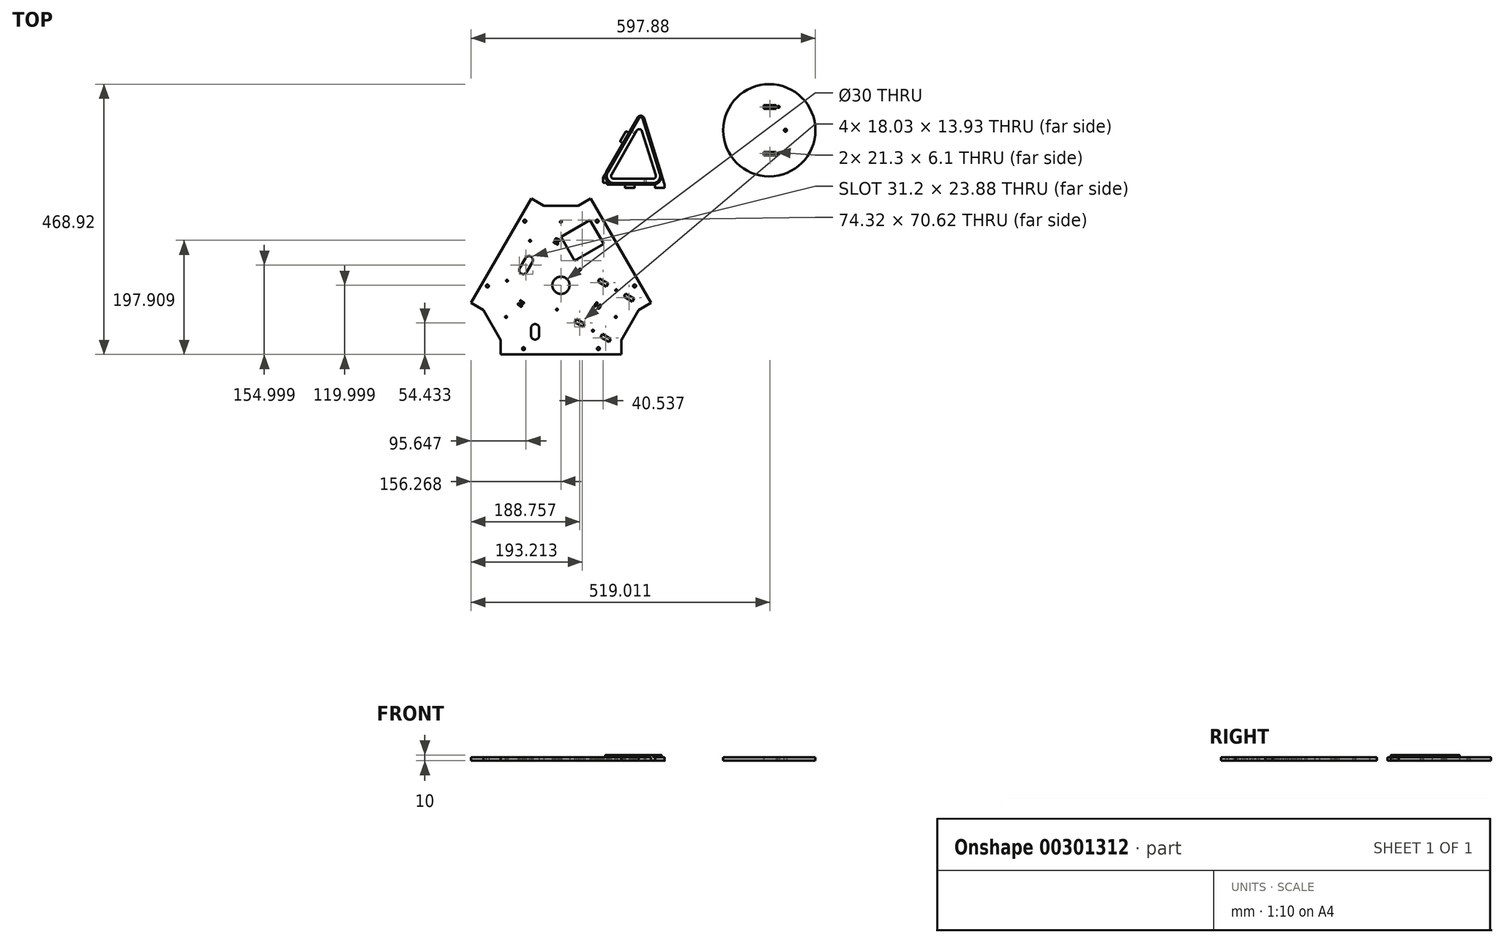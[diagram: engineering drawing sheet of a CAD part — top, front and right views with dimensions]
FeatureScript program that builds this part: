
annotation { "Feature Type Name" : "Feature", "Feature Type Description" : "" }
export const myFeature = defineFeature(function(context is Context, id is Id, definition is map)
    precondition{}
    {
        {
            var Q0;
            Q0=qCreatedBy(makeId("Top.planeOp"),FACE);
            var sketch = newSketch(context, id + "F0", { "sketchPlane" : qUnion([Q0])});
            skCircle(sketch, "E0", {"center": v(-173.6, -123.38) * mm, "radius": 80 * mm});
            skCircle(sketch, "E1", {"center": v(-45.84, -124.67) * mm, "radius": 2.5 * mm});
            skCircle(sketch, "E2", {"center": v(-110.84, -12.09) * mm, "radius": 2.5 * mm});
            skArc(sketch, "E3", {"start": v(-30.8, -243.38) * mm, "mid": v(-29.38, -242.8) * mm, "end": v(-28.8, -241.38) * mm});
            skLineSegment(sketch, "E4", {"start": v(-316.4, -243.38) * mm, "end": v(-30.8, -243.38) * mm});
            skArc(sketch, "E5", {"start": v(-318.4, -241.38) * mm, "mid": v(-317.81, -242.8) * mm, "end": v(-316.4, -243.38) * mm});
            skLineSegment(sketch, "E6", {"start": v(-318.4, -241.38) * mm, "end": v(-318.4, -221.41) * mm});
            skArc(sketch, "E7", {"start": v(-317.9, -220.55) * mm, "mid": v(-318.26, -220.91) * mm, "end": v(-318.4, -221.41) * mm});
            skLineSegment(sketch, "E8", {"start": v(-317.9, -220.55) * mm, "end": v(-299.77, -210.08) * mm});
            skLineSegment(sketch, "E9", {"start": v(-299.77, -210.08) * mm, "end": v(-311.77, -189.3) * mm});
            skLineSegment(sketch, "E10", {"start": v(-311.77, -189.3) * mm, "end": v(-329.9, -199.76) * mm});
            skArc(sketch, "E11", {"start": v(-330.9, -199.76) * mm, "mid": v(-330.4, -199.9) * mm, "end": v(-329.9, -199.76) * mm});
            skLineSegment(sketch, "E12", {"start": v(-348.19, -189.78) * mm, "end": v(-330.9, -199.76) * mm});
            skArc(sketch, "E13", {"start": v(-348.92, -187.05) * mm, "mid": v(-349.12, -188.57) * mm, "end": v(-348.19, -189.78) * mm});
            skLineSegment(sketch, "E14", {"start": v(-206.12, 60.29) * mm, "end": v(-348.92, -187.05) * mm});
            skLineSegment(sketch, "E15", {"start": v(-203.39, 61.02) * mm, "end": v(-186.1, 51.04) * mm});
            skArc(sketch, "E16", {"start": v(-185.6, 50.17) * mm, "mid": v(-185.73, 50.67) * mm, "end": v(-186.1, 51.04) * mm});
            skLineSegment(sketch, "E17", {"start": v(-185.6, 50.17) * mm, "end": v(-185.6, 29.24) * mm});
            skLineSegment(sketch, "E18", {"start": v(-185.6, 29.24) * mm, "end": v(-161.6, 29.24) * mm});
            skLineSegment(sketch, "E19", {"start": v(-161.6, 29.24) * mm, "end": v(-161.6, 50.17) * mm});
            skArc(sketch, "E20", {"start": v(-161.1, 51.04) * mm, "mid": v(-161.46, 50.67) * mm, "end": v(-161.6, 50.17) * mm});
            skLineSegment(sketch, "E21", {"start": v(-143.8, 61.02) * mm, "end": v(-161.1, 51.04) * mm});
            skLineSegment(sketch, "E22", {"start": v(1.72, -187.05) * mm, "end": v(-141.08, 60.29) * mm});
            skArc(sketch, "E23", {"start": v(1, -189.78) * mm, "mid": v(1.92, -188.57) * mm, "end": v(1.72, -187.05) * mm});
            skLineSegment(sketch, "E24", {"start": v(1, -189.78) * mm, "end": v(-16.3, -199.76) * mm});
            skArc(sketch, "E25", {"start": v(-17.3, -199.76) * mm, "mid": v(-16.8, -199.9) * mm, "end": v(-16.3, -199.76) * mm});
            skLineSegment(sketch, "E26", {"start": v(-17.3, -199.76) * mm, "end": v(-35.43, -189.3) * mm});
            skLineSegment(sketch, "E27", {"start": v(-35.43, -189.3) * mm, "end": v(-47.43, -210.08) * mm});
            skLineSegment(sketch, "E28", {"start": v(-47.43, -210.08) * mm, "end": v(-29.3, -220.55) * mm});
            skArc(sketch, "E29", {"start": v(-28.8, -221.41) * mm, "mid": v(-28.93, -220.91) * mm, "end": v(-29.3, -220.55) * mm});
            skLineSegment(sketch, "E30", {"start": v(-28.8, -241.38) * mm, "end": v(-28.8, -221.41) * mm});
            skCircle(sketch, "E31", {"center": v(-236.36, -12.09) * mm, "radius": 2.5 * mm});
            skCircle(sketch, "E32", {"center": v(-301.36, -124.67) * mm, "radius": 2.5 * mm});
            skCircle(sketch, "E33", {"center": v(-238.6, -233.38) * mm, "radius": 2.5 * mm});
            skCircle(sketch, "E34", {"center": v(-108.6, -233.38) * mm, "radius": 2.5 * mm});
            skCircle(sketch, "E35", {"center": v(-268.86, -178.38) * mm, "radius": 1.65 * mm});
            skCircle(sketch, "E36", {"center": v(-78.34, -178.38) * mm, "radius": 1.65 * mm});
            skCircle(sketch, "E37", {"center": v(-173.6, -13.38) * mm, "radius": 1.65 * mm});
            skArc(sketch, "E38", {"start": v(-141.08, 60.29) * mm, "mid": v(-142.29, 61.22) * mm, "end": v(-143.8, 61.02) * mm});
            skArc(sketch, "E39", {"start": v(-203.39, 61.02) * mm, "mid": v(-204.9, 61.22) * mm, "end": v(-206.12, 60.29) * mm});
            skCircle(sketch, "E40", {"center": v(-562.52, 74.64) * mm, "radius": 9 * mm});
            skLineSegment(sketch, "E41", {"start": v(-591.44, 65.5) * mm, "end": v(-551.64, 48) * mm});
            skArc(sketch, "E42", {"start": v(-591.44, 83.8) * mm, "mid": v(-597.42, 74.64) * mm, "end": v(-591.44, 65.5) * mm});
            skLineSegment(sketch, "E43", {"start": v(-551.64, 101.3) * mm, "end": v(-591.44, 83.8) * mm});
            skArc(sketch, "E44", {"start": v(-537.62, 92.14) * mm, "mid": v(-542.15, 100.52) * mm, "end": v(-551.64, 101.3) * mm});
            skLineSegment(sketch, "E45", {"start": v(-537.62, 57.14) * mm, "end": v(-537.62, 92.14) * mm});
            skArc(sketch, "E46", {"start": v(-551.64, 48) * mm, "mid": v(-542.15, 48.77) * mm, "end": v(-537.62, 57.14) * mm});
            skCircle(sketch, "E47", {"center": v(-547.62, 92.14) * mm, "radius": 2.5 * mm});
            skCircle(sketch, "E48", {"center": v(-587.42, 74.64) * mm, "radius": 2.5 * mm});
            skCircle(sketch, "E49", {"center": v(-547.62, 57.14) * mm, "radius": 2.5 * mm});
            skLineSegment(sketch, "E50", {"start": v(-547.62, 57.14) * mm, "end": v(-547.62, 59.64) * mm});
            skLineSegment(sketch, "E51", {"start": v(-547.62, 57.14) * mm, "end": v(-550.12, 57.14) * mm});
            skLineSegment(sketch, "E52", {"start": v(-547.62, 57.14) * mm, "end": v(-547.62, 54.64) * mm});
            skLineSegment(sketch, "E53", {"start": v(-547.62, 57.14) * mm, "end": v(-545.12, 57.14) * mm});
            skLineSegment(sketch, "E54", {"start": v(-547.62, 59.64) * mm, "end": v(-547.62, 62.14) * mm});
            skLineSegment(sketch, "E55", {"start": v(-550.12, 57.14) * mm, "end": v(-552.62, 57.14) * mm});
            skLineSegment(sketch, "E56", {"start": v(-547.62, 54.64) * mm, "end": v(-547.62, 52.14) * mm});
            skLineSegment(sketch, "E57", {"start": v(-545.12, 57.14) * mm, "end": v(-542.62, 57.14) * mm});
            skLineSegment(sketch, "E58", {"start": v(-547.62, 92.14) * mm, "end": v(-547.62, 94.64) * mm});
            skLineSegment(sketch, "E59", {"start": v(-547.62, 92.14) * mm, "end": v(-550.12, 92.14) * mm});
            skLineSegment(sketch, "E60", {"start": v(-547.62, 92.14) * mm, "end": v(-547.62, 89.64) * mm});
            skLineSegment(sketch, "E61", {"start": v(-547.62, 92.14) * mm, "end": v(-545.12, 92.14) * mm});
            skLineSegment(sketch, "E62", {"start": v(-547.62, 94.64) * mm, "end": v(-547.62, 97.14) * mm});
            skLineSegment(sketch, "E63", {"start": v(-550.12, 92.14) * mm, "end": v(-552.62, 92.14) * mm});
            skLineSegment(sketch, "E64", {"start": v(-547.62, 89.64) * mm, "end": v(-547.62, 87.14) * mm});
            skLineSegment(sketch, "E65", {"start": v(-545.12, 92.14) * mm, "end": v(-542.62, 92.14) * mm});
            skLineSegment(sketch, "E66", {"start": v(-587.42, 74.64) * mm, "end": v(-587.42, 77.14) * mm});
            skLineSegment(sketch, "E67", {"start": v(-587.42, 74.64) * mm, "end": v(-589.92, 74.64) * mm});
            skLineSegment(sketch, "E68", {"start": v(-587.42, 74.64) * mm, "end": v(-587.42, 72.14) * mm});
            skLineSegment(sketch, "E69", {"start": v(-587.42, 74.64) * mm, "end": v(-584.92, 74.64) * mm});
            skLineSegment(sketch, "E70", {"start": v(-587.42, 77.14) * mm, "end": v(-587.42, 79.64) * mm});
            skLineSegment(sketch, "E71", {"start": v(-589.92, 74.64) * mm, "end": v(-592.42, 74.64) * mm});
            skLineSegment(sketch, "E72", {"start": v(-587.42, 72.14) * mm, "end": v(-587.42, 69.64) * mm});
            skLineSegment(sketch, "E73", {"start": v(-584.92, 74.64) * mm, "end": v(-582.42, 74.64) * mm});
            skLineSegment(sketch, "E74", {"start": v(-562.52, 74.64) * mm, "end": v(-562.52, 77.14) * mm});
            skLineSegment(sketch, "E75", {"start": v(-562.52, 74.64) * mm, "end": v(-565.02, 74.64) * mm});
            skLineSegment(sketch, "E76", {"start": v(-562.52, 74.64) * mm, "end": v(-562.52, 72.14) * mm});
            skLineSegment(sketch, "E77", {"start": v(-562.52, 74.64) * mm, "end": v(-560.02, 74.64) * mm});
            skLineSegment(sketch, "E78", {"start": v(-562.52, 79.64) * mm, "end": v(-562.52, 86.14) * mm});
            skLineSegment(sketch, "E79", {"start": v(-567.52, 74.64) * mm, "end": v(-574.02, 74.64) * mm});
            skLineSegment(sketch, "E80", {"start": v(-562.52, 69.64) * mm, "end": v(-562.52, 63.14) * mm});
            skLineSegment(sketch, "E81", {"start": v(-557.52, 74.64) * mm, "end": v(-551.02, 74.64) * mm});
            skCircle(sketch, "E82", {"center": v(-570.44, -110.92) * mm, "radius": 15 * mm});
            skCircle(sketch, "E83", {"center": v(-442.68, -112.21) * mm, "radius": 2.5 * mm});
            skCircle(sketch, "E84", {"center": v(-507.68, 0.37) * mm, "radius": 2.5 * mm});
            skCircle(sketch, "E85", {"center": v(-633.2, 0.37) * mm, "radius": 2.5 * mm});
            skCircle(sketch, "E86", {"center": v(-698.2, -112.21) * mm, "radius": 2.5 * mm});
            skCircle(sketch, "E87", {"center": v(-635.44, -220.92) * mm, "radius": 2.5 * mm});
            skCircle(sketch, "E88", {"center": v(-505.44, -220.92) * mm, "radius": 2.5 * mm});
            skCircle(sketch, "E89", {"center": v(-665.7, -165.92) * mm, "radius": 1.65 * mm});
            skCircle(sketch, "E90", {"center": v(-475.18, -165.92) * mm, "radius": 1.65 * mm});
            skCircle(sketch, "E91", {"center": v(-570.44, -0.92) * mm, "radius": 1.65 * mm});
            skLineSegment(sketch, "E92", {"start": v(-414.17, -141.6) * mm, "end": v(-435.89, -154.13) * mm});
            skLineSegment(sketch, "E93", {"start": v(-435.89, -154.13) * mm, "end": v(-465.74, -205.84) * mm});
            skLineSegment(sketch, "E94", {"start": v(-465.74, -205.84) * mm, "end": v(-465.74, -230.92) * mm});
            skLineSegment(sketch, "E95", {"start": v(-675.14, -230.92) * mm, "end": v(-465.74, -230.92) * mm});
            skLineSegment(sketch, "E96", {"start": v(-675.14, -230.92) * mm, "end": v(-675.14, -205.84) * mm});
            skLineSegment(sketch, "E97", {"start": v(-675.14, -205.84) * mm, "end": v(-705, -154.13) * mm});
            skLineSegment(sketch, "E98", {"start": v(-705, -154.13) * mm, "end": v(-726.71, -141.6) * mm});
            skLineSegment(sketch, "E99", {"start": v(-622.01, 39.75) * mm, "end": v(-600.3, 27.21) * mm});
            skLineSegment(sketch, "E100", {"start": v(-600.3, 27.21) * mm, "end": v(-540.59, 27.21) * mm});
            skLineSegment(sketch, "E101", {"start": v(-483.9, -204.17) * mm, "end": v(-486.95, -209.45) * mm});
            skLineSegment(sketch, "E102", {"start": v(-498.89, -195.52) * mm, "end": v(-483.9, -204.17) * mm});
            skLineSegment(sketch, "E103", {"start": v(-501.94, -200.8) * mm, "end": v(-498.89, -195.52) * mm});
            skLineSegment(sketch, "E104", {"start": v(-486.95, -209.45) * mm, "end": v(-501.94, -200.8) * mm});
            skLineSegment(sketch, "E105", {"start": v(-528.94, -178.17) * mm, "end": v(-531.99, -183.45) * mm});
            skLineSegment(sketch, "E106", {"start": v(-543.92, -169.52) * mm, "end": v(-528.94, -178.17) * mm});
            skLineSegment(sketch, "E107", {"start": v(-546.97, -174.8) * mm, "end": v(-543.92, -169.52) * mm});
            skLineSegment(sketch, "E108", {"start": v(-531.99, -183.45) * mm, "end": v(-546.97, -174.8) * mm});
            skLineSegment(sketch, "E109", {"start": v(-443.37, -133.96) * mm, "end": v(-446.42, -139.24) * mm});
            skLineSegment(sketch, "E110", {"start": v(-458.35, -125.3) * mm, "end": v(-443.37, -133.96) * mm});
            skLineSegment(sketch, "E111", {"start": v(-461.4, -130.6) * mm, "end": v(-458.35, -125.3) * mm});
            skLineSegment(sketch, "E112", {"start": v(-446.42, -139.24) * mm, "end": v(-461.4, -130.6) * mm});
            skLineSegment(sketch, "E113", {"start": v(-488.4, -107.96) * mm, "end": v(-491.45, -113.24) * mm});
            skLineSegment(sketch, "E114", {"start": v(-503.38, -99.3) * mm, "end": v(-488.4, -107.96) * mm});
            skLineSegment(sketch, "E115", {"start": v(-506.43, -104.6) * mm, "end": v(-503.38, -99.3) * mm});
            skLineSegment(sketch, "E116", {"start": v(-491.45, -113.24) * mm, "end": v(-506.43, -104.6) * mm});
            skCircle(sketch, "E117", {"center": v(-515, -189.74) * mm, "radius": 1.65 * mm});
            skCircle(sketch, "E118", {"center": v(-474.47, -119.52) * mm, "radius": 1.65 * mm});
            skCircle(sketch, "E119", {"center": v(-537.46, -83.77) * mm, "radius": 1.5 * mm});
            skCircle(sketch, "E120", {"center": v(-577.46, -153.05) * mm, "radius": 1.5 * mm});
            skCircle(sketch, "E121", {"center": v(-624.07, -33.77) * mm, "radius": 1.5 * mm});
            skCircle(sketch, "E122", {"center": v(-664.07, -103.05) * mm, "radius": 1.5 * mm});
            skLineSegment(sketch, "E123", {"start": v(-570.66, -26.75) * mm, "end": v(-546.66, -68.32) * mm});
            skLineSegment(sketch, "E124", {"start": v(-546.66, -68.32) * mm, "end": v(-496.34, -39.27) * mm});
            skLineSegment(sketch, "E125", {"start": v(-496.34, -39.27) * mm, "end": v(-520.34, 2.3) * mm});
            skLineSegment(sketch, "E126", {"start": v(-520.34, 2.3) * mm, "end": v(-570.66, -26.75) * mm});
            skLineSegment(sketch, "E127", {"start": v(-632.13, -63.76) * mm, "end": v(-642.13, -81.08) * mm});
            skArc(sketch, "E128", {"start": v(-642.13, -81.08) * mm, "mid": v(-639.56, -90.64) * mm, "end": v(-630, -88.08) * mm});
            skLineSegment(sketch, "E129", {"start": v(-630, -88.08) * mm, "end": v(-620, -70.76) * mm});
            skArc(sketch, "E130", {"start": v(-620, -70.76) * mm, "mid": v(-622.56, -61.2) * mm, "end": v(-632.13, -63.76) * mm});
            skLineSegment(sketch, "E131", {"start": v(-509.93, -147.17) * mm, "end": v(-507.16, -143.01) * mm});
            skArc(sketch, "E132", {"start": v(-507.16, -143.01) * mm, "mid": v(-507.58, -140.93) * mm, "end": v(-509.66, -141.35) * mm});
            skLineSegment(sketch, "E133", {"start": v(-509.66, -141.35) * mm, "end": v(-512.43, -145.5) * mm});
            skArc(sketch, "E134", {"start": v(-512.43, -145.5) * mm, "mid": v(-512.01, -147.59) * mm, "end": v(-509.93, -147.17) * mm});
            skLineSegment(sketch, "E135", {"start": v(-503.83, -151.09) * mm, "end": v(-501.16, -146.86) * mm});
            skArc(sketch, "E136", {"start": v(-501.16, -146.86) * mm, "mid": v(-501.63, -144.79) * mm, "end": v(-503.7, -145.26) * mm});
            skLineSegment(sketch, "E137", {"start": v(-503.7, -145.26) * mm, "end": v(-506.37, -149.48) * mm});
            skArc(sketch, "E138", {"start": v(-506.37, -149.48) * mm, "mid": v(-505.9, -151.55) * mm, "end": v(-503.83, -151.09) * mm});
            skLineSegment(sketch, "E139", {"start": v(-641.1, -139.8) * mm, "end": v(-637.1, -142.8) * mm});
            skArc(sketch, "E140", {"start": v(-637.1, -142.8) * mm, "mid": v(-635, -142.5) * mm, "end": v(-635.3, -140.4) * mm});
            skLineSegment(sketch, "E141", {"start": v(-635.3, -140.4) * mm, "end": v(-639.31, -137.4) * mm});
            skArc(sketch, "E142", {"start": v(-639.31, -137.4) * mm, "mid": v(-641.41, -137.7) * mm, "end": v(-641.1, -139.8) * mm});
            skLineSegment(sketch, "E143", {"start": v(-644.8, -144.98) * mm, "end": v(-640.7, -147.85) * mm});
            skArc(sketch, "E144", {"start": v(-640.7, -147.85) * mm, "mid": v(-638.61, -147.48) * mm, "end": v(-638.98, -145.4) * mm});
            skLineSegment(sketch, "E145", {"start": v(-638.98, -145.4) * mm, "end": v(-643.07, -142.52) * mm});
            skArc(sketch, "E146", {"start": v(-643.07, -142.52) * mm, "mid": v(-645.16, -142.89) * mm, "end": v(-644.8, -144.98) * mm});
            skLineSegment(sketch, "E147", {"start": v(-581.94, -38.04) * mm, "end": v(-577.35, -40.01) * mm});
            skArc(sketch, "E148", {"start": v(-577.35, -40.01) * mm, "mid": v(-575.38, -39.23) * mm, "end": v(-576.16, -37.25) * mm});
            skLineSegment(sketch, "E149", {"start": v(-576.16, -37.25) * mm, "end": v(-580.76, -35.28) * mm});
            skArc(sketch, "E150", {"start": v(-580.76, -35.28) * mm, "mid": v(-582.73, -36.06) * mm, "end": v(-581.94, -38.04) * mm});
            skLineSegment(sketch, "E151", {"start": v(-579.39, -32.22) * mm, "end": v(-574.85, -34.33) * mm});
            skArc(sketch, "E152", {"start": v(-574.85, -34.33) * mm, "mid": v(-572.86, -33.6) * mm, "end": v(-573.6, -31.6) * mm});
            skLineSegment(sketch, "E153", {"start": v(-573.6, -31.6) * mm, "end": v(-578.12, -29.5) * mm});
            skArc(sketch, "E154", {"start": v(-578.12, -29.5) * mm, "mid": v(-580.12, -30.23) * mm, "end": v(-579.39, -32.22) * mm});
            skLineSegment(sketch, "E155", {"start": v(-622.01, 39.75) * mm, "end": v(-726.71, -141.6) * mm});
            skLineSegment(sketch, "E156", {"start": v(-414.17, -141.6) * mm, "end": v(-518.87, 39.75) * mm});
            skLineSegment(sketch, "E157", {"start": v(-540.59, 27.21) * mm, "end": v(-518.87, 39.75) * mm});
            skLineSegment(sketch, "E158", {"start": v(-442.68, -112.21) * mm, "end": v(-442.68, -109.71) * mm});
            skLineSegment(sketch, "E159", {"start": v(-442.68, -112.21) * mm, "end": v(-445.18, -112.21) * mm});
            skLineSegment(sketch, "E160", {"start": v(-442.68, -112.21) * mm, "end": v(-442.68, -114.71) * mm});
            skLineSegment(sketch, "E161", {"start": v(-442.68, -112.21) * mm, "end": v(-440.18, -112.21) * mm});
            skLineSegment(sketch, "E162", {"start": v(-442.68, -109.71) * mm, "end": v(-442.68, -107.21) * mm});
            skLineSegment(sketch, "E163", {"start": v(-445.18, -112.21) * mm, "end": v(-447.68, -112.21) * mm});
            skLineSegment(sketch, "E164", {"start": v(-442.68, -114.71) * mm, "end": v(-442.68, -117.21) * mm});
            skLineSegment(sketch, "E165", {"start": v(-440.18, -112.21) * mm, "end": v(-437.68, -112.21) * mm});
            skLineSegment(sketch, "E166", {"start": v(-507.68, 0.37) * mm, "end": v(-507.68, 2.87) * mm});
            skLineSegment(sketch, "E167", {"start": v(-507.68, 0.37) * mm, "end": v(-510.18, 0.37) * mm});
            skLineSegment(sketch, "E168", {"start": v(-507.68, 0.37) * mm, "end": v(-507.68, -2.13) * mm});
            skLineSegment(sketch, "E169", {"start": v(-507.68, 0.37) * mm, "end": v(-505.18, 0.37) * mm});
            skLineSegment(sketch, "E170", {"start": v(-507.68, 2.87) * mm, "end": v(-507.68, 5.37) * mm});
            skLineSegment(sketch, "E171", {"start": v(-510.18, 0.37) * mm, "end": v(-512.68, 0.37) * mm});
            skLineSegment(sketch, "E172", {"start": v(-507.68, -2.13) * mm, "end": v(-507.68, -4.63) * mm});
            skLineSegment(sketch, "E173", {"start": v(-505.18, 0.37) * mm, "end": v(-502.68, 0.37) * mm});
            skLineSegment(sketch, "E174", {"start": v(-633.2, 0.37) * mm, "end": v(-633.2, 2.87) * mm});
            skLineSegment(sketch, "E175", {"start": v(-633.2, 0.37) * mm, "end": v(-635.7, 0.37) * mm});
            skLineSegment(sketch, "E176", {"start": v(-633.2, 0.37) * mm, "end": v(-633.2, -2.13) * mm});
            skLineSegment(sketch, "E177", {"start": v(-633.2, 0.37) * mm, "end": v(-630.7, 0.37) * mm});
            skLineSegment(sketch, "E178", {"start": v(-633.2, 2.87) * mm, "end": v(-633.2, 5.37) * mm});
            skLineSegment(sketch, "E179", {"start": v(-635.7, 0.37) * mm, "end": v(-638.2, 0.37) * mm});
            skLineSegment(sketch, "E180", {"start": v(-633.2, -2.13) * mm, "end": v(-633.2, -4.63) * mm});
            skLineSegment(sketch, "E181", {"start": v(-630.7, 0.37) * mm, "end": v(-628.2, 0.37) * mm});
            skLineSegment(sketch, "E182", {"start": v(-698.2, -112.21) * mm, "end": v(-698.2, -109.71) * mm});
            skLineSegment(sketch, "E183", {"start": v(-698.2, -112.21) * mm, "end": v(-700.7, -112.21) * mm});
            skLineSegment(sketch, "E184", {"start": v(-698.2, -112.21) * mm, "end": v(-698.2, -114.71) * mm});
            skLineSegment(sketch, "E185", {"start": v(-698.2, -112.21) * mm, "end": v(-695.7, -112.21) * mm});
            skLineSegment(sketch, "E186", {"start": v(-698.2, -109.71) * mm, "end": v(-698.2, -107.21) * mm});
            skLineSegment(sketch, "E187", {"start": v(-700.7, -112.21) * mm, "end": v(-703.2, -112.21) * mm});
            skLineSegment(sketch, "E188", {"start": v(-698.2, -114.71) * mm, "end": v(-698.2, -117.21) * mm});
            skLineSegment(sketch, "E189", {"start": v(-695.7, -112.21) * mm, "end": v(-693.2, -112.21) * mm});
            skLineSegment(sketch, "E190", {"start": v(-635.44, -220.92) * mm, "end": v(-635.44, -218.42) * mm});
            skLineSegment(sketch, "E191", {"start": v(-635.44, -220.92) * mm, "end": v(-637.94, -220.92) * mm});
            skLineSegment(sketch, "E192", {"start": v(-635.44, -220.92) * mm, "end": v(-635.44, -223.42) * mm});
            skLineSegment(sketch, "E193", {"start": v(-635.44, -220.92) * mm, "end": v(-632.94, -220.92) * mm});
            skLineSegment(sketch, "E194", {"start": v(-635.44, -218.42) * mm, "end": v(-635.44, -215.92) * mm});
            skLineSegment(sketch, "E195", {"start": v(-637.94, -220.92) * mm, "end": v(-640.44, -220.92) * mm});
            skLineSegment(sketch, "E196", {"start": v(-635.44, -223.42) * mm, "end": v(-635.44, -225.92) * mm});
            skLineSegment(sketch, "E197", {"start": v(-632.94, -220.92) * mm, "end": v(-630.44, -220.92) * mm});
            skLineSegment(sketch, "E198", {"start": v(-505.44, -220.92) * mm, "end": v(-505.44, -218.42) * mm});
            skLineSegment(sketch, "E199", {"start": v(-505.44, -220.92) * mm, "end": v(-507.94, -220.92) * mm});
            skLineSegment(sketch, "E200", {"start": v(-505.44, -220.92) * mm, "end": v(-505.44, -223.42) * mm});
            skLineSegment(sketch, "E201", {"start": v(-505.44, -220.92) * mm, "end": v(-502.94, -220.92) * mm});
            skLineSegment(sketch, "E202", {"start": v(-505.44, -218.42) * mm, "end": v(-505.44, -215.92) * mm});
            skLineSegment(sketch, "E203", {"start": v(-507.94, -220.92) * mm, "end": v(-510.44, -220.92) * mm});
            skLineSegment(sketch, "E204", {"start": v(-505.44, -223.42) * mm, "end": v(-505.44, -225.92) * mm});
            skLineSegment(sketch, "E205", {"start": v(-502.94, -220.92) * mm, "end": v(-500.44, -220.92) * mm});
            skLineSegment(sketch, "E206", {"start": v(-570.44, -110.92) * mm, "end": v(-570.44, -108.42) * mm});
            skLineSegment(sketch, "E207", {"start": v(-570.44, -110.92) * mm, "end": v(-572.94, -110.92) * mm});
            skLineSegment(sketch, "E208", {"start": v(-570.44, -110.92) * mm, "end": v(-570.44, -113.42) * mm});
            skLineSegment(sketch, "E209", {"start": v(-570.44, -110.92) * mm, "end": v(-567.94, -110.92) * mm});
            skLineSegment(sketch, "E210", {"start": v(-570.44, -105.92) * mm, "end": v(-570.44, -93.42) * mm});
            skLineSegment(sketch, "E211", {"start": v(-575.44, -110.92) * mm, "end": v(-587.94, -110.92) * mm});
            skLineSegment(sketch, "E212", {"start": v(-570.44, -115.92) * mm, "end": v(-570.44, -128.42) * mm});
            skLineSegment(sketch, "E213", {"start": v(-565.44, -110.92) * mm, "end": v(-552.94, -110.92) * mm});
            skLineSegment(sketch, "E214", {"start": v(-515, -189.74) * mm, "end": v(-515, -187.24) * mm});
            skLineSegment(sketch, "E215", {"start": v(-515, -189.74) * mm, "end": v(-517.5, -189.74) * mm});
            skLineSegment(sketch, "E216", {"start": v(-515, -189.74) * mm, "end": v(-515, -192.24) * mm});
            skLineSegment(sketch, "E217", {"start": v(-515, -189.74) * mm, "end": v(-512.5, -189.74) * mm});
            skLineSegment(sketch, "E218", {"start": v(-515, -187.24) * mm, "end": v(-515, -185.59) * mm});
            skLineSegment(sketch, "E219", {"start": v(-517.5, -189.74) * mm, "end": v(-519.15, -189.74) * mm});
            skLineSegment(sketch, "E220", {"start": v(-515, -192.24) * mm, "end": v(-515, -193.89) * mm});
            skLineSegment(sketch, "E221", {"start": v(-512.5, -189.74) * mm, "end": v(-510.85, -189.74) * mm});
            skLineSegment(sketch, "E222", {"start": v(-474.47, -119.52) * mm, "end": v(-474.47, -117.02) * mm});
            skLineSegment(sketch, "E223", {"start": v(-474.47, -119.52) * mm, "end": v(-476.97, -119.52) * mm});
            skLineSegment(sketch, "E224", {"start": v(-474.47, -119.52) * mm, "end": v(-474.47, -122.02) * mm});
            skLineSegment(sketch, "E225", {"start": v(-474.47, -119.52) * mm, "end": v(-471.97, -119.52) * mm});
            skLineSegment(sketch, "E226", {"start": v(-474.47, -117.02) * mm, "end": v(-474.47, -115.37) * mm});
            skLineSegment(sketch, "E227", {"start": v(-476.97, -119.52) * mm, "end": v(-478.62, -119.52) * mm});
            skLineSegment(sketch, "E228", {"start": v(-474.47, -122.02) * mm, "end": v(-474.47, -123.67) * mm});
            skLineSegment(sketch, "E229", {"start": v(-471.97, -119.52) * mm, "end": v(-470.32, -119.52) * mm});
            skLineSegment(sketch, "E230", {"start": v(-537.46, -83.77) * mm, "end": v(-537.46, -81.27) * mm});
            skLineSegment(sketch, "E231", {"start": v(-537.46, -83.77) * mm, "end": v(-539.96, -83.77) * mm});
            skLineSegment(sketch, "E232", {"start": v(-537.46, -83.77) * mm, "end": v(-537.46, -86.27) * mm});
            skLineSegment(sketch, "E233", {"start": v(-537.46, -83.77) * mm, "end": v(-534.96, -83.77) * mm});
            skLineSegment(sketch, "E234", {"start": v(-537.46, -81.27) * mm, "end": v(-537.46, -79.77) * mm});
            skLineSegment(sketch, "E235", {"start": v(-539.96, -83.77) * mm, "end": v(-541.46, -83.77) * mm});
            skLineSegment(sketch, "E236", {"start": v(-537.46, -86.27) * mm, "end": v(-537.46, -87.77) * mm});
            skLineSegment(sketch, "E237", {"start": v(-534.96, -83.77) * mm, "end": v(-533.46, -83.77) * mm});
            skLineSegment(sketch, "E238", {"start": v(-577.46, -153.05) * mm, "end": v(-577.46, -150.55) * mm});
            skLineSegment(sketch, "E239", {"start": v(-577.46, -153.05) * mm, "end": v(-579.96, -153.05) * mm});
            skLineSegment(sketch, "E240", {"start": v(-577.46, -153.05) * mm, "end": v(-577.46, -155.55) * mm});
            skLineSegment(sketch, "E241", {"start": v(-577.46, -153.05) * mm, "end": v(-574.96, -153.05) * mm});
            skLineSegment(sketch, "E242", {"start": v(-577.46, -150.55) * mm, "end": v(-577.46, -149.05) * mm});
            skLineSegment(sketch, "E243", {"start": v(-579.96, -153.05) * mm, "end": v(-581.46, -153.05) * mm});
            skLineSegment(sketch, "E244", {"start": v(-577.46, -155.55) * mm, "end": v(-577.46, -157.05) * mm});
            skLineSegment(sketch, "E245", {"start": v(-574.96, -153.05) * mm, "end": v(-573.46, -153.05) * mm});
            skLineSegment(sketch, "E246", {"start": v(-624.07, -33.77) * mm, "end": v(-624.07, -31.27) * mm});
            skLineSegment(sketch, "E247", {"start": v(-624.07, -33.77) * mm, "end": v(-626.57, -33.77) * mm});
            skLineSegment(sketch, "E248", {"start": v(-624.07, -33.77) * mm, "end": v(-624.07, -36.27) * mm});
            skLineSegment(sketch, "E249", {"start": v(-624.07, -33.77) * mm, "end": v(-621.57, -33.77) * mm});
            skLineSegment(sketch, "E250", {"start": v(-624.07, -31.27) * mm, "end": v(-624.07, -29.77) * mm});
            skLineSegment(sketch, "E251", {"start": v(-626.57, -33.77) * mm, "end": v(-628.07, -33.77) * mm});
            skLineSegment(sketch, "E252", {"start": v(-624.07, -36.27) * mm, "end": v(-624.07, -37.77) * mm});
            skLineSegment(sketch, "E253", {"start": v(-621.57, -33.77) * mm, "end": v(-620.07, -33.77) * mm});
            skLineSegment(sketch, "E254", {"start": v(-664.07, -103.05) * mm, "end": v(-664.07, -100.55) * mm});
            skLineSegment(sketch, "E255", {"start": v(-664.07, -103.05) * mm, "end": v(-666.57, -103.05) * mm});
            skLineSegment(sketch, "E256", {"start": v(-664.07, -103.05) * mm, "end": v(-664.07, -105.55) * mm});
            skLineSegment(sketch, "E257", {"start": v(-664.07, -103.05) * mm, "end": v(-661.57, -103.05) * mm});
            skLineSegment(sketch, "E258", {"start": v(-664.07, -100.55) * mm, "end": v(-664.07, -99.05) * mm});
            skLineSegment(sketch, "E259", {"start": v(-666.57, -103.05) * mm, "end": v(-668.07, -103.05) * mm});
            skLineSegment(sketch, "E260", {"start": v(-664.07, -105.55) * mm, "end": v(-664.07, -107.05) * mm});
            skLineSegment(sketch, "E261", {"start": v(-661.57, -103.05) * mm, "end": v(-660.07, -103.05) * mm});
            skArc(sketch, "E262", {"start": v(-402.84, -69.04) * mm, "mid": v(-404.96, -69.92) * mm, "end": v(-405.84, -72.04) * mm});
            skArc(sketch, "E263", {"start": v(-357.84, -72.04) * mm, "mid": v(-358.71, -69.92) * mm, "end": v(-360.84, -69.04) * mm});
            skArc(sketch, "E264", {"start": v(-360.84, -139.04) * mm, "mid": v(-358.71, -138.16) * mm, "end": v(-357.84, -136.04) * mm});
            skArc(sketch, "E265", {"start": v(-405.84, -136.04) * mm, "mid": v(-404.96, -138.16) * mm, "end": v(-402.84, -139.04) * mm});
            skCircle(sketch, "E266", {"center": v(-361.99, -78.04) * mm, "radius": 1.75 * mm});
            skCircle(sketch, "E267", {"center": v(-401.99, -81.04) * mm, "radius": 1.75 * mm});
            skCircle(sketch, "E268", {"center": v(-373.81, -78.74) * mm, "radius": 7 * mm});
            skLineSegment(sketch, "E269", {"start": v(-401.84, -129.54) * mm, "end": v(-401.84, -130.54) * mm});
            skArc(sketch, "E270", {"start": v(-401.84, -130.54) * mm, "mid": v(-399.34, -133.04) * mm, "end": v(-396.84, -130.54) * mm});
            skLineSegment(sketch, "E271", {"start": v(-396.84, -130.54) * mm, "end": v(-396.84, -129.54) * mm});
            skArc(sketch, "E272", {"start": v(-396.84, -129.54) * mm, "mid": v(-399.34, -127.04) * mm, "end": v(-401.84, -129.54) * mm});
            skLineSegment(sketch, "E273", {"start": v(-366.84, -129.54) * mm, "end": v(-366.84, -130.54) * mm});
            skArc(sketch, "E274", {"start": v(-366.84, -130.54) * mm, "mid": v(-364.34, -133.04) * mm, "end": v(-361.84, -130.54) * mm});
            skLineSegment(sketch, "E275", {"start": v(-361.84, -130.54) * mm, "end": v(-361.84, -129.54) * mm});
            skArc(sketch, "E276", {"start": v(-361.84, -129.54) * mm, "mid": v(-364.34, -127.04) * mm, "end": v(-366.84, -129.54) * mm});
            skLineSegment(sketch, "E277", {"start": v(-360.84, -69.04) * mm, "end": v(-402.84, -69.04) * mm});
            skLineSegment(sketch, "E278", {"start": v(-357.84, -136.04) * mm, "end": v(-357.84, -72.04) * mm});
            skLineSegment(sketch, "E279", {"start": v(-402.84, -139.04) * mm, "end": v(-360.84, -139.04) * mm});
            skLineSegment(sketch, "E280", {"start": v(-405.84, -72.04) * mm, "end": v(-405.84, -136.04) * mm});
            skLineSegment(sketch, "E281", {"start": v(-361.99, -78.04) * mm, "end": v(-361.99, -75.54) * mm});
            skLineSegment(sketch, "E282", {"start": v(-361.99, -78.04) * mm, "end": v(-364.49, -78.04) * mm});
            skLineSegment(sketch, "E283", {"start": v(-361.99, -78.04) * mm, "end": v(-361.99, -80.54) * mm});
            skLineSegment(sketch, "E284", {"start": v(-361.99, -78.04) * mm, "end": v(-359.49, -78.04) * mm});
            skLineSegment(sketch, "E285", {"start": v(-361.99, -75.54) * mm, "end": v(-361.99, -73.79) * mm});
            skLineSegment(sketch, "E286", {"start": v(-364.49, -78.04) * mm, "end": v(-366.24, -78.04) * mm});
            skLineSegment(sketch, "E287", {"start": v(-361.99, -80.54) * mm, "end": v(-361.99, -82.29) * mm});
            skLineSegment(sketch, "E288", {"start": v(-359.49, -78.04) * mm, "end": v(-357.74, -78.04) * mm});
            skLineSegment(sketch, "E289", {"start": v(-401.99, -81.04) * mm, "end": v(-401.99, -78.54) * mm});
            skLineSegment(sketch, "E290", {"start": v(-401.99, -81.04) * mm, "end": v(-404.49, -81.04) * mm});
            skLineSegment(sketch, "E291", {"start": v(-401.99, -81.04) * mm, "end": v(-401.99, -83.54) * mm});
            skLineSegment(sketch, "E292", {"start": v(-401.99, -81.04) * mm, "end": v(-399.49, -81.04) * mm});
            skLineSegment(sketch, "E293", {"start": v(-401.99, -78.54) * mm, "end": v(-401.99, -76.79) * mm});
            skLineSegment(sketch, "E294", {"start": v(-404.49, -81.04) * mm, "end": v(-406.24, -81.04) * mm});
            skLineSegment(sketch, "E295", {"start": v(-401.99, -83.54) * mm, "end": v(-401.99, -85.29) * mm});
            skLineSegment(sketch, "E296", {"start": v(-399.49, -81.04) * mm, "end": v(-397.74, -81.04) * mm});
            skLineSegment(sketch, "E297", {"start": v(-373.81, -78.74) * mm, "end": v(-373.81, -76.24) * mm});
            skLineSegment(sketch, "E298", {"start": v(-373.81, -78.74) * mm, "end": v(-376.31, -78.74) * mm});
            skLineSegment(sketch, "E299", {"start": v(-373.81, -78.74) * mm, "end": v(-373.81, -81.24) * mm});
            skLineSegment(sketch, "E300", {"start": v(-373.81, -78.74) * mm, "end": v(-371.31, -78.74) * mm});
            skLineSegment(sketch, "E301", {"start": v(-373.81, -73.74) * mm, "end": v(-373.81, -69.24) * mm});
            skLineSegment(sketch, "E302", {"start": v(-378.81, -78.74) * mm, "end": v(-383.31, -78.74) * mm});
            skLineSegment(sketch, "E303", {"start": v(-373.81, -83.74) * mm, "end": v(-373.81, -88.24) * mm});
            skLineSegment(sketch, "E304", {"start": v(-368.81, -78.74) * mm, "end": v(-364.31, -78.74) * mm});
            skLineSegment(sketch, "E305", {"start": v(-399.34, -130.04) * mm, "end": v(-399.34, -127.54) * mm});
            skLineSegment(sketch, "E306", {"start": v(-399.34, -130.04) * mm, "end": v(-401.84, -130.04) * mm});
            skLineSegment(sketch, "E307", {"start": v(-399.34, -130.04) * mm, "end": v(-399.34, -132.54) * mm});
            skLineSegment(sketch, "E308", {"start": v(-399.34, -130.04) * mm, "end": v(-396.84, -130.04) * mm});
            skLineSegment(sketch, "E309", {"start": v(-399.34, -127.54) * mm, "end": v(-399.34, -125.04) * mm});
            skLineSegment(sketch, "E310", {"start": v(-401.84, -130.04) * mm, "end": v(-404.34, -130.04) * mm});
            skLineSegment(sketch, "E311", {"start": v(-399.34, -132.54) * mm, "end": v(-399.34, -135.04) * mm});
            skLineSegment(sketch, "E312", {"start": v(-396.84, -130.04) * mm, "end": v(-394.34, -130.04) * mm});
            skLineSegment(sketch, "E313", {"start": v(-364.34, -130.04) * mm, "end": v(-364.34, -127.54) * mm});
            skLineSegment(sketch, "E314", {"start": v(-364.34, -130.04) * mm, "end": v(-366.84, -130.04) * mm});
            skLineSegment(sketch, "E315", {"start": v(-364.34, -130.04) * mm, "end": v(-364.34, -132.54) * mm});
            skLineSegment(sketch, "E316", {"start": v(-364.34, -130.04) * mm, "end": v(-361.84, -130.04) * mm});
            skLineSegment(sketch, "E317", {"start": v(-364.34, -127.54) * mm, "end": v(-364.34, -125.04) * mm});
            skLineSegment(sketch, "E318", {"start": v(-366.84, -130.04) * mm, "end": v(-369.34, -130.04) * mm});
            skLineSegment(sketch, "E319", {"start": v(-364.34, -132.54) * mm, "end": v(-364.34, -135.04) * mm});
            skLineSegment(sketch, "E320", {"start": v(-361.84, -130.04) * mm, "end": v(-359.34, -130.04) * mm});
            skLineSegment(sketch, "E321", {"start": v(-442.5, 63.73) * mm, "end": v(-426.07, 63.73) * mm});
            skLineSegment(sketch, "E322", {"start": v(-442.5, 58.23) * mm, "end": v(-442.5, 63.73) * mm});
            skLineSegment(sketch, "E323", {"start": v(-459.5, 58.23) * mm, "end": v(-442.5, 58.23) * mm});
            skLineSegment(sketch, "E324", {"start": v(-459.5, 63.73) * mm, "end": v(-459.5, 58.23) * mm});
            skLineSegment(sketch, "E325", {"start": v(-476.46, 63.73) * mm, "end": v(-459.5, 63.73) * mm});
            skArc(sketch, "E326", {"start": v(-479, 75.16) * mm, "mid": v(-482.32, 68.43) * mm, "end": v(-476.46, 63.73) * mm});
            skLineSegment(sketch, "E327", {"start": v(-433.34, 96.45) * mm, "end": v(-479, 75.16) * mm});
            skLineSegment(sketch, "E328", {"start": v(-435.67, 101.44) * mm, "end": v(-433.34, 96.45) * mm});
            skLineSegment(sketch, "E329", {"start": v(-416.63, 110.31) * mm, "end": v(-435.67, 101.44) * mm});
            skLineSegment(sketch, "E330", {"start": v(-414.3, 105.33) * mm, "end": v(-416.63, 110.31) * mm});
            skLineSegment(sketch, "E331", {"start": v(-411.59, 106.6) * mm, "end": v(-414.3, 105.33) * mm});
            skLineSegment(sketch, "E332", {"start": v(-411.59, 106.6) * mm, "end": v(-409.05, 101.16) * mm});
            skLineSegment(sketch, "E333", {"start": v(-409.05, 101.16) * mm, "end": v(-410.12, 100.66) * mm});
            skLineSegment(sketch, "E334", {"start": v(-410.12, 100.66) * mm, "end": v(-408.94, 98.12) * mm});
            skLineSegment(sketch, "E335", {"start": v(-408.94, 98.12) * mm, "end": v(-407.87, 98.62) * mm});
            skLineSegment(sketch, "E336", {"start": v(-407.87, 98.62) * mm, "end": v(-405.34, 93.18) * mm});
            skLineSegment(sketch, "E337", {"start": v(-405.34, 93.18) * mm, "end": v(-402.48, 94.51) * mm});
            skLineSegment(sketch, "E338", {"start": v(-402.48, 94.51) * mm, "end": v(-405.02, 99.95) * mm});
            skLineSegment(sketch, "E339", {"start": v(-405.02, 99.95) * mm, "end": v(-403.95, 100.45) * mm});
            skLineSegment(sketch, "E340", {"start": v(-403.95, 100.45) * mm, "end": v(-405.13, 102.99) * mm});
            skLineSegment(sketch, "E341", {"start": v(-405.13, 102.99) * mm, "end": v(-406.2, 102.49) * mm});
            skLineSegment(sketch, "E342", {"start": v(-406.2, 102.49) * mm, "end": v(-408.73, 107.93) * mm});
            skLineSegment(sketch, "E343", {"start": v(-374.95, 123.68) * mm, "end": v(-408.73, 107.93) * mm});
            skArc(sketch, "E344", {"start": v(-373.52, 122.78) * mm, "mid": v(-373.99, 123.62) * mm, "end": v(-374.95, 123.68) * mm});
            skLineSegment(sketch, "E345", {"start": v(-373.52, 64.73) * mm, "end": v(-373.52, 122.78) * mm});
            skArc(sketch, "E346", {"start": v(-374.52, 63.73) * mm, "mid": v(-373.82, 64.02) * mm, "end": v(-373.52, 64.73) * mm});
            skLineSegment(sketch, "E347", {"start": v(-390.5, 63.73) * mm, "end": v(-374.52, 63.73) * mm});
            skLineSegment(sketch, "E348", {"start": v(-390.5, 58.23) * mm, "end": v(-390.5, 63.73) * mm});
            skLineSegment(sketch, "E349", {"start": v(-407.5, 58.23) * mm, "end": v(-390.5, 58.23) * mm});
            skLineSegment(sketch, "E350", {"start": v(-407.5, 63.73) * mm, "end": v(-407.5, 58.23) * mm});
            skLineSegment(sketch, "E351", {"start": v(-422.92, 63.73) * mm, "end": v(-407.5, 63.73) * mm});
            skLineSegment(sketch, "E352", {"start": v(-422.92, 63.73) * mm, "end": v(-422.92, 69.73) * mm});
            skLineSegment(sketch, "E353", {"start": v(-422.92, 69.73) * mm, "end": v(-421.74, 69.73) * mm});
            skLineSegment(sketch, "E354", {"start": v(-421.74, 69.73) * mm, "end": v(-421.74, 72.53) * mm});
            skLineSegment(sketch, "E355", {"start": v(-421.74, 72.53) * mm, "end": v(-422.92, 72.53) * mm});
            skLineSegment(sketch, "E356", {"start": v(-422.92, 72.53) * mm, "end": v(-422.92, 78.53) * mm});
            skLineSegment(sketch, "E357", {"start": v(-422.92, 78.53) * mm, "end": v(-426.07, 78.53) * mm});
            skLineSegment(sketch, "E358", {"start": v(-426.07, 78.53) * mm, "end": v(-426.07, 72.53) * mm});
            skLineSegment(sketch, "E359", {"start": v(-426.07, 72.53) * mm, "end": v(-427.24, 72.53) * mm});
            skLineSegment(sketch, "E360", {"start": v(-427.24, 72.53) * mm, "end": v(-427.24, 69.73) * mm});
            skLineSegment(sketch, "E361", {"start": v(-427.24, 69.73) * mm, "end": v(-426.07, 69.73) * mm});
            skLineSegment(sketch, "E362", {"start": v(-426.07, 69.73) * mm, "end": v(-426.07, 63.73) * mm});
            skCircle(sketch, "E363", {"center": v(-180.83, 158) * mm, "radius": 2.55 * mm});
            skLineSegment(sketch, "E364", {"start": v(-197.05, 195.49) * mm, "end": v(-197.05, 201.59) * mm});
            skLineSegment(sketch, "E365", {"start": v(-197.05, 201.59) * mm, "end": v(-218.35, 201.59) * mm});
            skLineSegment(sketch, "E366", {"start": v(-218.35, 201.59) * mm, "end": v(-218.35, 195.49) * mm});
            skLineSegment(sketch, "E367", {"start": v(-218.35, 195.49) * mm, "end": v(-197.05, 195.49) * mm});
            skCircle(sketch, "E368", {"center": v(-208.83, 158) * mm, "radius": 80 * mm});
            skCircle(sketch, "E369", {"center": v(-192.62, 198.54) * mm, "radius": 1.6 * mm});
            skArc(sketch, "E370", {"start": v(-321.18, 72.46) * mm, "mid": v(-319.75, 70.3) * mm, "end": v(-317.3, 69.46) * mm});
            skLineSegment(sketch, "E371", {"start": v(-332.28, 72.15) * mm, "end": v(-337.44, 66.99) * mm});
            skLineSegment(sketch, "E372", {"start": v(-337.44, 66.99) * mm, "end": v(-333.13, 62.67) * mm});
            skLineSegment(sketch, "E373", {"start": v(-333.13, 62.67) * mm, "end": v(-327.97, 67.84) * mm});
            skLineSegment(sketch, "E374", {"start": v(-327.97, 67.84) * mm, "end": v(-332.28, 72.15) * mm});
            skCircle(sketch, "E375", {"center": v(-328.06, 72.06) * mm, "radius": 1.65 * mm});
            skLineSegment(sketch, "E376", {"start": v(-287.8, 69.46) * mm, "end": v(-317.3, 69.46) * mm});
            skArc(sketch, "E377", {"start": v(-287.8, 57.46) * mm, "mid": v(-281.8, 63.46) * mm, "end": v(-287.8, 69.46) * mm});
            skLineSegment(sketch, "E378", {"start": v(-332.8, 57.46) * mm, "end": v(-287.8, 57.46) * mm});
            skArc(sketch, "E379", {"start": v(-321.18, 72.46) * mm, "mid": v(-342.28, 76.81) * mm, "end": v(-332.8, 57.46) * mm});
            skLineSegment(sketch, "E380", {"start": v(-328.06, 72.06) * mm, "end": v(-328.06, 74.56) * mm});
            skLineSegment(sketch, "E381", {"start": v(-328.06, 72.06) * mm, "end": v(-330.56, 72.06) * mm});
            skLineSegment(sketch, "E382", {"start": v(-328.06, 72.06) * mm, "end": v(-328.06, 69.56) * mm});
            skLineSegment(sketch, "E383", {"start": v(-328.06, 72.06) * mm, "end": v(-325.56, 72.06) * mm});
            skLineSegment(sketch, "E384", {"start": v(-328.06, 74.56) * mm, "end": v(-328.06, 76.21) * mm});
            skLineSegment(sketch, "E385", {"start": v(-330.56, 72.06) * mm, "end": v(-332.2, 72.06) * mm});
            skLineSegment(sketch, "E386", {"start": v(-328.06, 69.56) * mm, "end": v(-328.06, 67.91) * mm});
            skLineSegment(sketch, "E387", {"start": v(-325.56, 72.06) * mm, "end": v(-323.9, 72.06) * mm});
            skLineSegment(sketch, "E388", {"start": v(-340.57, -29.13) * mm, "end": v(-338.8, -29.13) * mm});
            skLineSegment(sketch, "E389", {"start": v(-338.8, -29.13) * mm, "end": v(-338.8, -24.2) * mm});
            skLineSegment(sketch, "E390", {"start": v(-338.8, -24.2) * mm, "end": v(-338.74, -22.6) * mm});
            skLineSegment(sketch, "E391", {"start": v(-338.74, -22.6) * mm, "end": v(-338.74, -20.47) * mm});
            skFitSpline(sketch, "E392", {"points": [v(-338.74, -20.47) * mm, v(-338.74, -19.9) * mm, v(-338.35, -19.53) * mm, v(-337.78, -19.53) * mm]});
            skLineSegment(sketch, "E393", {"start": v(-337.78, -19.53) * mm, "end": v(-334.74, -19.53) * mm});
            skFitSpline(sketch, "E394", {"points": [v(-334.74, -19.53) * mm, v(-334.18, -19.53) * mm, v(-333.78, -19.95) * mm, v(-333.78, -20.49) * mm]});
            skLineSegment(sketch, "E395", {"start": v(-333.78, -20.49) * mm, "end": v(-333.78, -21.66) * mm});
            skFitSpline(sketch, "E396", {"points": [v(-333.78, -21.66) * mm, v(-333.78, -22.28) * mm, v(-334.18, -22.6) * mm, v(-334.69, -22.6) * mm]});
            skLineSegment(sketch, "E397", {"start": v(-334.69, -22.6) * mm, "end": v(-336.85, -22.6) * mm});
            skLineSegment(sketch, "E398", {"start": v(-336.85, -22.6) * mm, "end": v(-336.85, -24.2) * mm});
            skLineSegment(sketch, "E399", {"start": v(-336.85, -24.2) * mm, "end": v(-334.48, -24.2) * mm});
            skFitSpline(sketch, "E400", {"points": [v(-334.48, -24.2) * mm, v(-334.04, -24.27) * mm, v(-333.75, -24.55) * mm, v(-333.75, -25.12) * mm]});
            skLineSegment(sketch, "E401", {"start": v(-333.75, -25.12) * mm, "end": v(-333.76, -29.13) * mm});
            skLineSegment(sketch, "E402", {"start": v(-333.76, -29.13) * mm, "end": v(-331.95, -29.13) * mm});
            skLineSegment(sketch, "E403", {"start": v(-331.95, -29.13) * mm, "end": v(-331.95, -24.87) * mm});
            skFitSpline(sketch, "E404", {"points": [v(-331.95, -24.87) * mm, v(-331.95, -24.45) * mm, v(-332.22, -24.05) * mm, v(-332.5, -23.71) * mm]});
            skFitSpline(sketch, "E405", {"points": [v(-332.5, -23.71) * mm, v(-332.18, -23.37) * mm, v(-331.91, -22.86) * mm, v(-331.93, -22.25) * mm]});
            skLineSegment(sketch, "E406", {"start": v(-331.93, -22.25) * mm, "end": v(-331.93, -20.23) * mm});
            skFitSpline(sketch, "E407", {"points": [v(-331.93, -20.23) * mm, v(-331.93, -18.9) * mm, v(-332.97, -17.91) * mm, v(-334.3, -17.91) * mm]});
            skLineSegment(sketch, "E408", {"start": v(-334.3, -17.91) * mm, "end": v(-338.14, -17.91) * mm});
            skFitSpline(sketch, "E409", {"points": [v(-338.14, -17.91) * mm, v(-339.48, -17.91) * mm, v(-340.57, -18.9) * mm, v(-340.57, -20.23) * mm]});
            skLineSegment(sketch, "E410", {"start": v(-340.57, -20.23) * mm, "end": v(-340.57, -29.13) * mm});
            skArc(sketch, "E411", {"start": v(-361.24, -20.57) * mm, "mid": v(-361.54, -19.86) * mm, "end": v(-362.24, -19.57) * mm});
            skLineSegment(sketch, "E412", {"start": v(-361.24, -20.57) * mm, "end": v(-361.24, -29.19) * mm});
            skLineSegment(sketch, "E413", {"start": v(-361.24, -29.19) * mm, "end": v(-359.5, -29.19) * mm});
            skLineSegment(sketch, "E414", {"start": v(-359.5, -29.19) * mm, "end": v(-359.5, -20.57) * mm});
            skArc(sketch, "E415", {"start": v(-358.5, -19.57) * mm, "mid": v(-359.2, -19.86) * mm, "end": v(-359.5, -20.57) * mm});
            skLineSegment(sketch, "E416", {"start": v(-358.5, -19.57) * mm, "end": v(-355.73, -19.57) * mm});
            skLineSegment(sketch, "E417", {"start": v(-355.73, -19.57) * mm, "end": v(-355.73, -17.93) * mm});
            skLineSegment(sketch, "E418", {"start": v(-355.73, -17.93) * mm, "end": v(-365.02, -17.93) * mm});
            skLineSegment(sketch, "E419", {"start": v(-365.02, -17.93) * mm, "end": v(-365.02, -19.57) * mm});
            skLineSegment(sketch, "E420", {"start": v(-365.02, -19.57) * mm, "end": v(-362.24, -19.57) * mm});
            skLineSegment(sketch, "E421", {"start": v(-387.19, -20.31) * mm, "end": v(-387.19, -26.8) * mm});
            skFitSpline(sketch, "E422", {"points": [v(-387.19, -26.8) * mm, v(-387.19, -27.94) * mm, v(-386.38, -28.9) * mm, v(-385.3, -29.14) * mm]});
            skLineSegment(sketch, "E423", {"start": v(-385.3, -29.14) * mm, "end": v(-385.3, -29.15) * mm});
            skLineSegment(sketch, "E424", {"start": v(-385.3, -29.15) * mm, "end": v(-385.24, -29.15) * mm});
            skFitSpline(sketch, "E425", {"points": [v(-385.24, -29.15) * mm, v(-385.1, -29.18) * mm, v(-384.95, -29.2) * mm, v(-384.8, -29.2) * mm]});
            skLineSegment(sketch, "E426", {"start": v(-384.8, -29.2) * mm, "end": v(-381.4, -29.2) * mm});
            skFitSpline(sketch, "E427", {"points": [v(-381.4, -29.2) * mm, v(-381.26, -29.2) * mm, v(-381.11, -29.18) * mm, v(-380.97, -29.15) * mm]});
            skLineSegment(sketch, "E428", {"start": v(-380.97, -29.15) * mm, "end": v(-379.02, -29.15) * mm});
            skLineSegment(sketch, "E429", {"start": v(-379.02, -29.15) * mm, "end": v(-379.02, -27.48) * mm});
            skLineSegment(sketch, "E430", {"start": v(-379.02, -27.48) * mm, "end": v(-384.57, -27.48) * mm});
            skFitSpline(sketch, "E431", {"points": [v(-384.57, -27.48) * mm, v(-384.98, -27.48) * mm, v(-385.3, -27.15) * mm, v(-385.3, -26.74) * mm]});
            skLineSegment(sketch, "E432", {"start": v(-385.3, -26.74) * mm, "end": v(-385.3, -24.34) * mm});
            skArc(sketch, "E433", {"start": v(-384.8, -23.84) * mm, "mid": v(-385.16, -23.99) * mm, "end": v(-385.3, -24.34) * mm});
            skLineSegment(sketch, "E434", {"start": v(-384.8, -23.84) * mm, "end": v(-379.02, -23.84) * mm});
            skLineSegment(sketch, "E435", {"start": v(-379.02, -23.84) * mm, "end": v(-379.02, -22.17) * mm});
            skLineSegment(sketch, "E436", {"start": v(-379.02, -22.17) * mm, "end": v(-384.8, -22.17) * mm});
            skArc(sketch, "E437", {"start": v(-385.3, -21.67) * mm, "mid": v(-385.16, -22.02) * mm, "end": v(-384.8, -22.17) * mm});
            skLineSegment(sketch, "E438", {"start": v(-385.3, -21.67) * mm, "end": v(-385.3, -20.33) * mm});
            skFitSpline(sketch, "E439", {"points": [v(-385.3, -20.33) * mm, v(-385.3, -19.93) * mm, v(-384.98, -19.6) * mm, v(-384.57, -19.6) * mm]});
            skLineSegment(sketch, "E440", {"start": v(-384.57, -19.6) * mm, "end": v(-379.02, -19.6) * mm});
            skLineSegment(sketch, "E441", {"start": v(-379.02, -19.6) * mm, "end": v(-379.02, -17.92) * mm});
            skLineSegment(sketch, "E442", {"start": v(-379.02, -17.92) * mm, "end": v(-384.96, -17.92) * mm});
            skFitSpline(sketch, "E443", {"points": [v(-384.96, -17.92) * mm, v(-386.1, -17.9) * mm, v(-387.19, -18.91) * mm, v(-387.19, -20.31) * mm]});
            skLineSegment(sketch, "E444", {"start": v(-421.93, -19.53) * mm, "end": v(-415.36, -19.53) * mm});
            skFitSpline(sketch, "E445", {"points": [v(-415.36, -19.53) * mm, v(-414.17, -19.55) * mm, v(-414.17, -20.03) * mm, v(-415.36, -20.99) * mm]});
            skFitSpline(sketch, "E446", {"points": [v(-415.36, -20.99) * mm, v(-416.54, -21.94) * mm, v(-418.44, -23.5) * mm, v(-421.05, -25.67) * mm]});
            skFitSpline(sketch, "E447", {"points": [v(-421.05, -25.67) * mm, v(-422.7, -27.25) * mm, v(-421.65, -29.07) * mm, v(-420.06, -29.13) * mm]});
            skLineSegment(sketch, "E448", {"start": v(-420.06, -29.13) * mm, "end": v(-412.6, -29.13) * mm});
            skLineSegment(sketch, "E449", {"start": v(-412.6, -29.13) * mm, "end": v(-412.6, -27.56) * mm});
            skLineSegment(sketch, "E450", {"start": v(-412.6, -27.56) * mm, "end": v(-418.89, -27.52) * mm});
            skFitSpline(sketch, "E451", {"points": [v(-418.89, -27.52) * mm, v(-419.29, -27.53) * mm, v(-419.99, -27.28) * mm, v(-419.3, -26.48) * mm]});
            skFitSpline(sketch, "E452", {"points": [v(-419.3, -26.48) * mm, v(-418.35, -25.74) * mm, v(-416.4, -24.12) * mm, v(-413.45, -21.6) * mm]});
            skFitSpline(sketch, "E453", {"points": [v(-413.45, -21.6) * mm, v(-412.33, -20.55) * mm, v(-412.13, -18.26) * mm, v(-414.25, -17.92) * mm]});
            skLineSegment(sketch, "E454", {"start": v(-414.25, -17.92) * mm, "end": v(-421.93, -17.87) * mm});
            skLineSegment(sketch, "E455", {"start": v(-421.93, -17.87) * mm, "end": v(-421.93, -19.53) * mm});
            skLineSegment(sketch, "E456", {"start": v(-403.07, -20.27) * mm, "end": v(-403.07, -26.85) * mm});
            skFitSpline(sketch, "E457", {"points": [v(-403.07, -26.85) * mm, v(-403.07, -27.25) * mm, v(-403.4, -27.58) * mm, v(-403.8, -27.58) * mm]});
            skLineSegment(sketch, "E458", {"start": v(-403.8, -27.58) * mm, "end": v(-407.71, -27.58) * mm});
            skFitSpline(sketch, "E459", {"points": [v(-407.71, -27.58) * mm, v(-408.12, -27.58) * mm, v(-408.44, -27.25) * mm, v(-408.44, -26.85) * mm]});
            skLineSegment(sketch, "E460", {"start": v(-408.44, -26.85) * mm, "end": v(-408.44, -20.27) * mm});
            skFitSpline(sketch, "E461", {"points": [v(-408.44, -20.27) * mm, v(-408.44, -19.87) * mm, v(-408.12, -19.54) * mm, v(-407.71, -19.54) * mm]});
            skLineSegment(sketch, "E462", {"start": v(-407.71, -19.54) * mm, "end": v(-406.8, -19.54) * mm});
            skLineSegment(sketch, "E463", {"start": v(-406.8, -19.54) * mm, "end": v(-406.8, -17.95) * mm});
            skLineSegment(sketch, "E464", {"start": v(-406.8, -17.95) * mm, "end": v(-408, -17.95) * mm});
            skFitSpline(sketch, "E465", {"points": [v(-408, -17.95) * mm, v(-409.3, -17.95) * mm, v(-410.35, -19) * mm, v(-410.35, -20.3) * mm]});
            skLineSegment(sketch, "E466", {"start": v(-410.35, -20.3) * mm, "end": v(-410.35, -26.82) * mm});
            skFitSpline(sketch, "E467", {"points": [v(-410.35, -26.82) * mm, v(-410.35, -28.1) * mm, v(-409.3, -29.17) * mm, v(-408, -29.17) * mm]});
            skLineSegment(sketch, "E468", {"start": v(-408, -29.17) * mm, "end": v(-403.56, -29.17) * mm});
            skFitSpline(sketch, "E469", {"points": [v(-403.56, -29.17) * mm, v(-402.26, -29.17) * mm, v(-401.2, -28.1) * mm, v(-401.2, -26.82) * mm]});
            skLineSegment(sketch, "E470", {"start": v(-401.2, -26.82) * mm, "end": v(-401.2, -20.3) * mm});
            skFitSpline(sketch, "E471", {"points": [v(-401.2, -20.3) * mm, v(-401.2, -19) * mm, v(-402.26, -17.95) * mm, v(-403.56, -17.95) * mm]});
            skLineSegment(sketch, "E472", {"start": v(-403.56, -17.95) * mm, "end": v(-404.63, -17.95) * mm});
            skLineSegment(sketch, "E473", {"start": v(-404.63, -17.95) * mm, "end": v(-404.63, -19.54) * mm});
            skLineSegment(sketch, "E474", {"start": v(-404.63, -19.54) * mm, "end": v(-403.8, -19.54) * mm});
            skFitSpline(sketch, "E475", {"points": [v(-403.8, -19.54) * mm, v(-403.4, -19.54) * mm, v(-403.07, -19.87) * mm, v(-403.07, -20.27) * mm]});
            skLineSegment(sketch, "E476", {"start": v(-330.7, -34.52) * mm, "end": v(-420.7, -34.52) * mm});
            skArc(sketch, "E477", {"start": v(-420.7, -34.52) * mm, "mid": v(-423.7, -35.5) * mm, "end": v(-425.5, -38.09) * mm});
            skArc(sketch, "E478", {"start": v(-427.42, -39.52) * mm, "mid": v(-426.22, -39.12) * mm, "end": v(-425.5, -38.09) * mm});
            skLineSegment(sketch, "E479", {"start": v(-454.2, -39.52) * mm, "end": v(-427.42, -39.52) * mm});
            skLineSegment(sketch, "E480", {"start": v(-454.2, -39.52) * mm, "end": v(-454.2, -36.52) * mm});
            skLineSegment(sketch, "E481", {"start": v(-454.2, -36.52) * mm, "end": v(-460, -36.52) * mm});
            skLineSegment(sketch, "E482", {"start": v(-460, -36.52) * mm, "end": v(-460, -29.52) * mm});
            skLineSegment(sketch, "E483", {"start": v(-460, -29.52) * mm, "end": v(-454.2, -29.52) * mm});
            skLineSegment(sketch, "E484", {"start": v(-454.2, -29.52) * mm, "end": v(-454.2, -28.02) * mm});
            skLineSegment(sketch, "E485", {"start": v(-454.2, -28.02) * mm, "end": v(-449.2, -28.02) * mm});
            skLineSegment(sketch, "E486", {"start": v(-449.2, -28.02) * mm, "end": v(-449.2, -29.2) * mm});
            skLineSegment(sketch, "E487", {"start": v(-449.2, -29.2) * mm, "end": v(-446.4, -29.2) * mm});
            skLineSegment(sketch, "E488", {"start": v(-446.4, -29.2) * mm, "end": v(-446.4, -28.02) * mm});
            skLineSegment(sketch, "E489", {"start": v(-446.4, -28.02) * mm, "end": v(-439.9, -28.02) * mm});
            skLineSegment(sketch, "E490", {"start": v(-439.9, -28.02) * mm, "end": v(-439.9, -24.87) * mm});
            skLineSegment(sketch, "E491", {"start": v(-439.9, -24.87) * mm, "end": v(-446.4, -24.87) * mm});
            skLineSegment(sketch, "E492", {"start": v(-446.4, -24.87) * mm, "end": v(-446.4, -23.7) * mm});
            skLineSegment(sketch, "E493", {"start": v(-446.4, -23.7) * mm, "end": v(-449.2, -23.7) * mm});
            skLineSegment(sketch, "E494", {"start": v(-449.2, -23.7) * mm, "end": v(-449.2, -24.87) * mm});
            skLineSegment(sketch, "E495", {"start": v(-449.2, -24.87) * mm, "end": v(-454.2, -24.87) * mm});
            skLineSegment(sketch, "E496", {"start": v(-454.2, -24.87) * mm, "end": v(-454.2, -19.63) * mm});
            skLineSegment(sketch, "E497", {"start": v(-454.2, -19.63) * mm, "end": v(-458, -19.63) * mm});
            skArc(sketch, "E498", {"start": v(-460, -17.63) * mm, "mid": v(-459.42, -19.05) * mm, "end": v(-458, -19.63) * mm});
            skLineSegment(sketch, "E499", {"start": v(-460, -17.63) * mm, "end": v(-460, -6.63) * mm});
            skArc(sketch, "E500", {"start": v(-458, -4.63) * mm, "mid": v(-459.42, -5.22) * mm, "end": v(-460, -6.63) * mm});
            skLineSegment(sketch, "E501", {"start": v(-458, -4.63) * mm, "end": v(-454.2, -4.63) * mm});
            skLineSegment(sketch, "E502", {"start": v(-454.2, -4.63) * mm, "end": v(-454.2, 34.48) * mm});
            skArc(sketch, "E503", {"start": v(-450.2, 38.48) * mm, "mid": v(-453.04, 37.31) * mm, "end": v(-454.2, 34.48) * mm});
            skLineSegment(sketch, "E504", {"start": v(-302.46, 38.48) * mm, "end": v(-450.2, 38.48) * mm});
            skArc(sketch, "E505", {"start": v(-298.46, 34.48) * mm, "mid": v(-299.63, 37.31) * mm, "end": v(-302.46, 38.48) * mm});
            skLineSegment(sketch, "E506", {"start": v(-298.46, 34.48) * mm, "end": v(-298.46, -4.63) * mm});
            skLineSegment(sketch, "E507", {"start": v(-298.46, -4.63) * mm, "end": v(-294.66, -4.63) * mm});
            skArc(sketch, "E508", {"start": v(-292.66, -6.63) * mm, "mid": v(-293.25, -5.22) * mm, "end": v(-294.66, -4.63) * mm});
            skLineSegment(sketch, "E509", {"start": v(-292.66, -6.63) * mm, "end": v(-292.66, -17.63) * mm});
            skArc(sketch, "E510", {"start": v(-294.66, -19.63) * mm, "mid": v(-293.25, -19.05) * mm, "end": v(-292.66, -17.63) * mm});
            skLineSegment(sketch, "E511", {"start": v(-294.66, -19.63) * mm, "end": v(-298.46, -19.63) * mm});
            skLineSegment(sketch, "E512", {"start": v(-298.46, -19.63) * mm, "end": v(-298.46, -24.87) * mm});
            skLineSegment(sketch, "E513", {"start": v(-298.46, -24.87) * mm, "end": v(-304.46, -24.87) * mm});
            skLineSegment(sketch, "E514", {"start": v(-304.46, -24.87) * mm, "end": v(-304.46, -23.7) * mm});
            skLineSegment(sketch, "E515", {"start": v(-304.46, -23.7) * mm, "end": v(-307.26, -23.7) * mm});
            skLineSegment(sketch, "E516", {"start": v(-307.26, -23.7) * mm, "end": v(-307.26, -24.87) * mm});
            skLineSegment(sketch, "E517", {"start": v(-307.26, -24.87) * mm, "end": v(-313.76, -24.87) * mm});
            skLineSegment(sketch, "E518", {"start": v(-313.76, -24.87) * mm, "end": v(-313.76, -28.02) * mm});
            skLineSegment(sketch, "E519", {"start": v(-313.76, -28.02) * mm, "end": v(-307.26, -28.02) * mm});
            skLineSegment(sketch, "E520", {"start": v(-307.26, -28.02) * mm, "end": v(-307.26, -29.2) * mm});
            skLineSegment(sketch, "E521", {"start": v(-307.26, -29.2) * mm, "end": v(-304.46, -29.2) * mm});
            skLineSegment(sketch, "E522", {"start": v(-304.46, -29.2) * mm, "end": v(-304.46, -28.02) * mm});
            skLineSegment(sketch, "E523", {"start": v(-304.46, -28.02) * mm, "end": v(-298.46, -28.02) * mm});
            skLineSegment(sketch, "E524", {"start": v(-298.46, -28.02) * mm, "end": v(-298.46, -29.52) * mm});
            skLineSegment(sketch, "E525", {"start": v(-298.46, -29.52) * mm, "end": v(-292.66, -29.52) * mm});
            skLineSegment(sketch, "E526", {"start": v(-292.66, -29.52) * mm, "end": v(-292.66, -36.52) * mm});
            skLineSegment(sketch, "E527", {"start": v(-292.66, -36.52) * mm, "end": v(-298.46, -36.52) * mm});
            skLineSegment(sketch, "E528", {"start": v(-298.46, -36.52) * mm, "end": v(-298.46, -39.52) * mm});
            skLineSegment(sketch, "E529", {"start": v(-324, -39.52) * mm, "end": v(-298.46, -39.52) * mm});
            skArc(sketch, "E530", {"start": v(-325.92, -38.09) * mm, "mid": v(-325.2, -39.12) * mm, "end": v(-324, -39.52) * mm});
            skArc(sketch, "E531", {"start": v(-325.92, -38.09) * mm, "mid": v(-327.72, -35.5) * mm, "end": v(-330.7, -34.52) * mm});
            skCircle(sketch, "E532", {"center": v(-324.46, -9.02) * mm, "radius": 4 * mm});
            skCircle(sketch, "E533", {"center": v(-324.46, 7.48) * mm, "radius": 5.25 * mm});
            skCircle(sketch, "E534", {"center": v(-324.46, 23.98) * mm, "radius": 6.5 * mm});
            skLineSegment(sketch, "E535", {"start": v(-448.6, 27.38) * mm, "end": v(-448.6, -12.42) * mm});
            skLineSegment(sketch, "E536", {"start": v(-448.6, -12.42) * mm, "end": v(-350.3, -12.42) * mm});
            skLineSegment(sketch, "E537", {"start": v(-350.3, -12.42) * mm, "end": v(-350.3, 27.38) * mm});
            skLineSegment(sketch, "E538", {"start": v(-350.3, 27.38) * mm, "end": v(-448.6, 27.38) * mm});
            skCircle(sketch, "E539", {"center": v(-304.46, -12.52) * mm, "radius": 1.75 * mm});
            skCircle(sketch, "E540", {"center": v(-445.96, -20.02) * mm, "radius": 1.75 * mm});
            skCircle(sketch, "E541", {"center": v(-304.46, 27.48) * mm, "radius": 1.75 * mm});
            skCircle(sketch, "E542", {"center": v(-445.96, 34.98) * mm, "radius": 1.75 * mm});
            skLineSegment(sketch, "E543", {"start": v(-350.21, -29.15) * mm, "end": v(-346, -29.15) * mm});
            skLineSegment(sketch, "E544", {"start": v(-346, -29.15) * mm, "end": v(-347.7, -23.59) * mm});
            skArc(sketch, "E545", {"start": v(-347.7, -23.59) * mm, "mid": v(-348.17, -23.23) * mm, "end": v(-348.65, -23.6) * mm});
            skLineSegment(sketch, "E546", {"start": v(-348.65, -23.6) * mm, "end": v(-350.21, -29.15) * mm});
            skLineSegment(sketch, "E547", {"start": v(-392.3, -26.96) * mm, "end": v(-395.12, -19.2) * mm});
            skFitSpline(sketch, "E548", {"points": [v(-395.12, -19.2) * mm, v(-395.44, -18.52) * mm, v(-395.93, -17.66) * mm, v(-397.46, -17.96) * mm]});
            skFitSpline(sketch, "E549", {"points": [v(-397.46, -17.96) * mm, v(-398.17, -18.1) * mm, v(-398.83, -18.73) * mm, v(-398.9, -19.27) * mm]});
            skLineSegment(sketch, "E550", {"start": v(-398.9, -19.27) * mm, "end": v(-398.9, -29.22) * mm});
            skLineSegment(sketch, "E551", {"start": v(-398.9, -29.22) * mm, "end": v(-397.08, -29.22) * mm});
            skLineSegment(sketch, "E552", {"start": v(-397.08, -29.22) * mm, "end": v(-397.08, -21.62) * mm});
            skArc(sketch, "E553", {"start": v(-396.11, -21.45) * mm, "mid": v(-396.67, -21.13) * mm, "end": v(-397.08, -21.62) * mm});
            skLineSegment(sketch, "E554", {"start": v(-396.11, -21.45) * mm, "end": v(-393.87, -27.48) * mm});
            skFitSpline(sketch, "E555", {"points": [v(-393.87, -27.48) * mm, v(-393.46, -29) * mm, v(-390.75, -29.9) * mm, v(-389.72, -27.84) * mm]});
            skFitSpline(sketch, "E556", {"points": [v(-389.72, -27.84) * mm, v(-389.59, -27.57) * mm, v(-389.43, -27.24) * mm, v(-389.45, -26.71) * mm]});
            skLineSegment(sketch, "E557", {"start": v(-389.45, -26.71) * mm, "end": v(-389.45, -17.89) * mm});
            skLineSegment(sketch, "E558", {"start": v(-389.45, -17.89) * mm, "end": v(-391.27, -17.89) * mm});
            skLineSegment(sketch, "E559", {"start": v(-391.27, -17.89) * mm, "end": v(-391.27, -26.8) * mm});
            skFitSpline(sketch, "E560", {"points": [v(-391.27, -26.8) * mm, v(-391.5, -27.41) * mm, v(-391.9, -27.64) * mm, v(-392.3, -26.96) * mm]});
            skLineSegment(sketch, "E561", {"start": v(-376.7, -20.31) * mm, "end": v(-376.7, -22.18) * mm});
            skFitSpline(sketch, "E562", {"points": [v(-376.7, -22.18) * mm, v(-376.67, -23.4) * mm, v(-375.75, -23.94) * mm, v(-374.71, -23.97) * mm]});
            skLineSegment(sketch, "E563", {"start": v(-374.71, -23.97) * mm, "end": v(-370, -23.97) * mm});
            skFitSpline(sketch, "E564", {"points": [v(-370, -23.97) * mm, v(-369.27, -23.97) * mm, v(-369, -24.57) * mm, v(-369, -24.93) * mm]});
            skLineSegment(sketch, "E565", {"start": v(-369, -24.93) * mm, "end": v(-369, -26.77) * mm});
            skFitSpline(sketch, "E566", {"points": [v(-369, -26.77) * mm, v(-369, -27.18) * mm, v(-369.34, -27.5) * mm, v(-369.74, -27.5) * mm]});
            skLineSegment(sketch, "E567", {"start": v(-369.74, -27.5) * mm, "end": v(-376.61, -27.5) * mm});
            skLineSegment(sketch, "E568", {"start": v(-376.61, -27.5) * mm, "end": v(-376.61, -29.18) * mm});
            skLineSegment(sketch, "E569", {"start": v(-376.61, -29.18) * mm, "end": v(-369.66, -29.18) * mm});
            skFitSpline(sketch, "E570", {"points": [v(-369.66, -29.18) * mm, v(-368.18, -29.21) * mm, v(-367.34, -28.13) * mm, v(-367.34, -26.8) * mm]});
            skLineSegment(sketch, "E571", {"start": v(-367.34, -26.8) * mm, "end": v(-367.34, -24.55) * mm});
            skFitSpline(sketch, "E572", {"points": [v(-367.34, -24.55) * mm, v(-367.38, -22.94) * mm, v(-368.26, -22.37) * mm, v(-369.58, -22.37) * mm]});
            skLineSegment(sketch, "E573", {"start": v(-369.58, -22.37) * mm, "end": v(-373.91, -22.37) * mm});
            skFitSpline(sketch, "E574", {"points": [v(-373.91, -22.37) * mm, v(-374.48, -22.39) * mm, v(-374.82, -21.86) * mm, v(-374.82, -21.5) * mm]});
            skLineSegment(sketch, "E575", {"start": v(-374.82, -21.5) * mm, "end": v(-374.82, -20.33) * mm});
            skFitSpline(sketch, "E576", {"points": [v(-374.82, -20.33) * mm, v(-374.82, -19.93) * mm, v(-374.49, -19.6) * mm, v(-374.08, -19.6) * mm]});
            skLineSegment(sketch, "E577", {"start": v(-374.08, -19.6) * mm, "end": v(-367.6, -19.6) * mm});
            skLineSegment(sketch, "E578", {"start": v(-367.6, -19.6) * mm, "end": v(-367.6, -17.92) * mm});
            skLineSegment(sketch, "E579", {"start": v(-367.6, -17.92) * mm, "end": v(-374.47, -17.92) * mm});
            skFitSpline(sketch, "E580", {"points": [v(-374.47, -17.92) * mm, v(-375.74, -17.9) * mm, v(-376.7, -18.6) * mm, v(-376.7, -20.31) * mm]});
            skLineSegment(sketch, "E581", {"start": v(-351.82, -29.15) * mm, "end": v(-349.28, -20.74) * mm});
            skFitSpline(sketch, "E582", {"points": [v(-349.28, -20.74) * mm, v(-349.04, -20.11) * mm, v(-348.85, -19.58) * mm, v(-348.26, -19.56) * mm]});
            skFitSpline(sketch, "E583", {"points": [v(-348.26, -19.56) * mm, v(-347.54, -19.54) * mm, v(-347.34, -20.12) * mm, v(-347.13, -20.74) * mm]});
            skLineSegment(sketch, "E584", {"start": v(-347.13, -20.74) * mm, "end": v(-344.54, -29.15) * mm});
            skLineSegment(sketch, "E585", {"start": v(-344.54, -29.15) * mm, "end": v(-342.78, -29.15) * mm});
            skLineSegment(sketch, "E586", {"start": v(-342.78, -29.15) * mm, "end": v(-345.5, -20) * mm});
            skFitSpline(sketch, "E587", {"points": [v(-345.5, -20) * mm, v(-346.12, -18.23) * mm, v(-347.42, -17.9) * mm, v(-348.21, -17.84) * mm]});
            skFitSpline(sketch, "E588", {"points": [v(-348.21, -17.84) * mm, v(-349.07, -17.82) * mm, v(-350.23, -18.2) * mm, v(-350.83, -20) * mm]});
            skLineSegment(sketch, "E589", {"start": v(-350.83, -20) * mm, "end": v(-353.55, -29.15) * mm});
            skLineSegment(sketch, "E590", {"start": v(-353.55, -29.15) * mm, "end": v(-351.82, -29.15) * mm});
            skLineSegment(sketch, "E591", {"start": v(-445.96, 34.98) * mm, "end": v(-445.96, 37.48) * mm});
            skLineSegment(sketch, "E592", {"start": v(-445.96, 34.98) * mm, "end": v(-448.46, 34.98) * mm});
            skLineSegment(sketch, "E593", {"start": v(-445.96, 34.98) * mm, "end": v(-445.96, 32.48) * mm});
            skLineSegment(sketch, "E594", {"start": v(-445.96, 34.98) * mm, "end": v(-443.46, 34.98) * mm});
            skLineSegment(sketch, "E595", {"start": v(-445.96, 37.48) * mm, "end": v(-445.96, 39.23) * mm});
            skLineSegment(sketch, "E596", {"start": v(-448.46, 34.98) * mm, "end": v(-450.2, 34.98) * mm});
            skLineSegment(sketch, "E597", {"start": v(-445.96, 32.48) * mm, "end": v(-445.96, 30.73) * mm});
            skLineSegment(sketch, "E598", {"start": v(-443.46, 34.98) * mm, "end": v(-441.7, 34.98) * mm});
            skLineSegment(sketch, "E599", {"start": v(-304.46, 27.48) * mm, "end": v(-304.46, 29.98) * mm});
            skLineSegment(sketch, "E600", {"start": v(-304.46, 27.48) * mm, "end": v(-306.96, 27.48) * mm});
            skLineSegment(sketch, "E601", {"start": v(-304.46, 27.48) * mm, "end": v(-304.46, 24.98) * mm});
            skLineSegment(sketch, "E602", {"start": v(-304.46, 27.48) * mm, "end": v(-301.96, 27.48) * mm});
            skLineSegment(sketch, "E603", {"start": v(-304.46, 29.98) * mm, "end": v(-304.46, 31.73) * mm});
            skLineSegment(sketch, "E604", {"start": v(-306.96, 27.48) * mm, "end": v(-308.7, 27.48) * mm});
            skLineSegment(sketch, "E605", {"start": v(-304.46, 24.98) * mm, "end": v(-304.46, 23.23) * mm});
            skLineSegment(sketch, "E606", {"start": v(-301.96, 27.48) * mm, "end": v(-300.2, 27.48) * mm});
            skLineSegment(sketch, "E607", {"start": v(-445.96, -20.02) * mm, "end": v(-445.96, -17.52) * mm});
            skLineSegment(sketch, "E608", {"start": v(-445.96, -20.02) * mm, "end": v(-448.46, -20.02) * mm});
            skLineSegment(sketch, "E609", {"start": v(-445.96, -20.02) * mm, "end": v(-445.96, -22.52) * mm});
            skLineSegment(sketch, "E610", {"start": v(-445.96, -20.02) * mm, "end": v(-443.46, -20.02) * mm});
            skLineSegment(sketch, "E611", {"start": v(-445.96, -17.52) * mm, "end": v(-445.96, -15.77) * mm});
            skLineSegment(sketch, "E612", {"start": v(-448.46, -20.02) * mm, "end": v(-450.2, -20.02) * mm});
            skLineSegment(sketch, "E613", {"start": v(-445.96, -22.52) * mm, "end": v(-445.96, -24.27) * mm});
            skLineSegment(sketch, "E614", {"start": v(-443.46, -20.02) * mm, "end": v(-441.7, -20.02) * mm});
            skLineSegment(sketch, "E615", {"start": v(-304.46, -12.52) * mm, "end": v(-304.46, -10.02) * mm});
            skLineSegment(sketch, "E616", {"start": v(-304.46, -12.52) * mm, "end": v(-306.96, -12.52) * mm});
            skLineSegment(sketch, "E617", {"start": v(-304.46, -12.52) * mm, "end": v(-304.46, -15.02) * mm});
            skLineSegment(sketch, "E618", {"start": v(-304.46, -12.52) * mm, "end": v(-301.96, -12.52) * mm});
            skLineSegment(sketch, "E619", {"start": v(-304.46, -10.02) * mm, "end": v(-304.46, -8.27) * mm});
            skLineSegment(sketch, "E620", {"start": v(-306.96, -12.52) * mm, "end": v(-308.7, -12.52) * mm});
            skLineSegment(sketch, "E621", {"start": v(-304.46, -15.02) * mm, "end": v(-304.46, -16.77) * mm});
            skLineSegment(sketch, "E622", {"start": v(-301.96, -12.52) * mm, "end": v(-300.2, -12.52) * mm});
            skLineSegment(sketch, "E623", {"start": v(-324.46, 23.98) * mm, "end": v(-324.46, 26.48) * mm});
            skLineSegment(sketch, "E624", {"start": v(-324.46, 23.98) * mm, "end": v(-326.96, 23.98) * mm});
            skLineSegment(sketch, "E625", {"start": v(-324.46, 23.98) * mm, "end": v(-324.46, 21.48) * mm});
            skLineSegment(sketch, "E626", {"start": v(-324.46, 23.98) * mm, "end": v(-321.96, 23.98) * mm});
            skLineSegment(sketch, "E627", {"start": v(-324.46, 28.98) * mm, "end": v(-324.46, 32.98) * mm});
            skLineSegment(sketch, "E628", {"start": v(-329.46, 23.98) * mm, "end": v(-333.46, 23.98) * mm});
            skLineSegment(sketch, "E629", {"start": v(-324.46, 18.98) * mm, "end": v(-324.46, 14.98) * mm});
            skLineSegment(sketch, "E630", {"start": v(-319.46, 23.98) * mm, "end": v(-315.46, 23.98) * mm});
            skLineSegment(sketch, "E631", {"start": v(-324.46, 7.48) * mm, "end": v(-324.46, 9.98) * mm});
            skLineSegment(sketch, "E632", {"start": v(-324.46, 7.48) * mm, "end": v(-326.96, 7.48) * mm});
            skLineSegment(sketch, "E633", {"start": v(-324.46, 7.48) * mm, "end": v(-324.46, 4.98) * mm});
            skLineSegment(sketch, "E634", {"start": v(-324.46, 7.48) * mm, "end": v(-321.96, 7.48) * mm});
            skLineSegment(sketch, "E635", {"start": v(-324.46, 12.48) * mm, "end": v(-324.46, 15.23) * mm});
            skLineSegment(sketch, "E636", {"start": v(-329.46, 7.48) * mm, "end": v(-332.2, 7.48) * mm});
            skLineSegment(sketch, "E637", {"start": v(-324.46, 2.48) * mm, "end": v(-324.46, -0.27) * mm});
            skLineSegment(sketch, "E638", {"start": v(-319.46, 7.48) * mm, "end": v(-316.7, 7.48) * mm});
            skLineSegment(sketch, "E639", {"start": v(-324.46, -9.02) * mm, "end": v(-324.46, -6.52) * mm});
            skLineSegment(sketch, "E640", {"start": v(-324.46, -9.02) * mm, "end": v(-326.96, -9.02) * mm});
            skLineSegment(sketch, "E641", {"start": v(-324.46, -9.02) * mm, "end": v(-324.46, -11.52) * mm});
            skLineSegment(sketch, "E642", {"start": v(-324.46, -9.02) * mm, "end": v(-321.96, -9.02) * mm});
            skLineSegment(sketch, "E643", {"start": v(-324.46, -4.02) * mm, "end": v(-324.46, -2.52) * mm});
            skLineSegment(sketch, "E644", {"start": v(-329.46, -9.02) * mm, "end": v(-330.96, -9.02) * mm});
            skLineSegment(sketch, "E645", {"start": v(-324.46, -14.02) * mm, "end": v(-324.46, -15.52) * mm});
            skLineSegment(sketch, "E646", {"start": v(-319.46, -9.02) * mm, "end": v(-317.96, -9.02) * mm});
            skArc(sketch, "E647", {"start": v(48.5, -12.79) * mm, "mid": v(48.66, -13) * mm, "end": v(48.87, -13.18) * mm});
            skArc(sketch, "E648", {"start": v(46.79, -5.72) * mm, "mid": v(47.23, -9.36) * mm, "end": v(48.5, -12.79) * mm});
            skArc(sketch, "E649", {"start": v(46.79, -5.72) * mm, "mid": v(46.63, -5.18) * mm, "end": v(46.21, -4.82) * mm});
            skLineSegment(sketch, "E650", {"start": v(45.98, -4.7) * mm, "end": v(46.21, -4.82) * mm});
            skArc(sketch, "E651", {"start": v(45.4, -3.68) * mm, "mid": v(45.53, -4.29) * mm, "end": v(45.98, -4.7) * mm});
            skArc(sketch, "E652", {"start": v(49.9, 5.95) * mm, "mid": v(46.88, 1.5) * mm, "end": v(45.4, -3.68) * mm});
            skArc(sketch, "E653", {"start": v(51.05, 6.17) * mm, "mid": v(50.44, 6.24) * mm, "end": v(49.9, 5.95) * mm});
            skLineSegment(sketch, "E654", {"start": v(51.28, 6.06) * mm, "end": v(51.05, 6.17) * mm});
            skArc(sketch, "E655", {"start": v(51.28, 6.06) * mm, "mid": v(51.83, 5.97) * mm, "end": v(52.35, 6.2) * mm});
            skArc(sketch, "E656", {"start": v(72.44, 6.02) * mm, "mid": v(62.43, 9.8) * mm, "end": v(52.35, 6.2) * mm});
            skArc(sketch, "E657", {"start": v(72.79, 5.26) * mm, "mid": v(72.7, 5.68) * mm, "end": v(72.44, 6.02) * mm});
            skLineSegment(sketch, "E658", {"start": v(72.79, -16.65) * mm, "end": v(72.79, 5.26) * mm});
            skArc(sketch, "E659", {"start": v(72.44, -17.4) * mm, "mid": v(72.7, -17.06) * mm, "end": v(72.79, -16.65) * mm});
            skArc(sketch, "E660", {"start": v(62.15, -21.2) * mm, "mid": v(67.64, -20.24) * mm, "end": v(72.44, -17.4) * mm});
            skArc(sketch, "E661", {"start": v(61.63, -21.04) * mm, "mid": v(61.88, -21.15) * mm, "end": v(62.15, -21.2) * mm});
            skLineSegment(sketch, "E662", {"start": v(48.87, -13.18) * mm, "end": v(61.63, -21.04) * mm});
            skCircle(sketch, "E663", {"center": v(66.6, 4.97) * mm, "radius": 1.55 * mm});
            skCircle(sketch, "E664", {"center": v(50.79, -5.7) * mm, "radius": 1.55 * mm});
            skCircle(sketch, "E665", {"center": v(66.6, -16.36) * mm, "radius": 1.55 * mm});
            skCircle(sketch, "E666", {"center": v(62.29, -5.7) * mm, "radius": 6 * mm});
            skLineSegment(sketch, "E667", {"start": v(-622.31, -185.22) * mm, "end": v(-622.31, -198.23) * mm});
            skArc(sketch, "E668", {"start": v(-622.31, -198.23) * mm, "mid": v(-615.31, -205.23) * mm, "end": v(-608.31, -198.23) * mm});
            skLineSegment(sketch, "E669", {"start": v(-608.31, -198.23) * mm, "end": v(-608.31, -185.22) * mm});
            skArc(sketch, "E670", {"start": v(-608.31, -185.22) * mm, "mid": v(-615.31, -178.22) * mm, "end": v(-622.31, -185.22) * mm});
            skPoint(sketch, "E671", {"position": v(-426.15, 105.88) * mm});
            skPoint(sketch, "E672", {"position": v(-424.5, 78.53) * mm});
            skPoint(sketch, "E673", {"position": v(-197.05, 198.54) * mm});
            skLineSegment(sketch, "E674", {"start": v(-208.83, 158) * mm, "end": v(-128.83, 158) * mm, "construction": true});
            skCircle(sketch, "E675.MirrorC", {"center": v(-192.62, 117.46) * mm, "radius": 1.6 * mm});
            skLineSegment(sketch, "E676.MirrorCS", {"start": v(-197.05, 114.41) * mm, "end": v(-218.35, 114.41) * mm});
            skLineSegment(sketch, "E677.MirrorCS", {"start": v(-218.35, 114.41) * mm, "end": v(-218.35, 120.51) * mm});
            skLineSegment(sketch, "E678.MirrorCS", {"start": v(-218.35, 120.51) * mm, "end": v(-197.05, 120.51) * mm});
            skLineSegment(sketch, "E679.MirrorCS", {"start": v(-197.05, 120.51) * mm, "end": v(-197.05, 114.41) * mm});
            skPoint(sketch, "E680", {"position": v(-373.52, 63.73) * mm});
            skPoint(sketch, "E681", {"position": v(-373.52, 124.35) * mm});
            skPoint(sketch, "E682", {"position": v(-503.52, 63.73) * mm});
            skSolve(sketch);
        }
        {
            var Q0;
            Q0=qCreatedBy(makeId("Top.planeOp"),FACE);
            var sketch = newSketch(context, id + "F1", { "sketchPlane" : qUnion([Q0])});
            skLineSegment(sketch, "E683.0", {"start": v(-197.05, 201.59) * mm, "end": v(-218.35, 201.59) * mm});
            skLineSegment(sketch, "E683.1", {"start": v(-218.35, 120.51) * mm, "end": v(-197.05, 120.51) * mm});
            skLineSegment(sketch, "E683.2", {"start": v(-197.05, 114.41) * mm, "end": v(-218.35, 114.41) * mm});
            skCircle(sketch, "E683.3", {"center": v(-208.83, 158) * mm, "radius": 80 * mm});
            skLineSegment(sketch, "E683.4", {"start": v(-218.35, 195.49) * mm, "end": v(-197.05, 195.49) * mm});
            skCircle(sketch, "E683.6", {"center": v(-180.83, 158) * mm, "radius": 2.55 * mm});
            skCircle(sketch, "E683.7", {"center": v(-192.62, 198.54) * mm, "radius": 1.6 * mm});
            skCircle(sketch, "E683.8", {"center": v(-192.62, 117.46) * mm, "radius": 1.6 * mm});
            skLineSegment(sketch, "E683.9", {"start": v(-197.05, 195.49) * mm, "end": v(-197.05, 201.59) * mm});
            skLineSegment(sketch, "E683.10", {"start": v(-197.05, 120.51) * mm, "end": v(-197.05, 114.41) * mm});
            skLineSegment(sketch, "E683.11", {"start": v(-218.35, 114.41) * mm, "end": v(-218.35, 120.51) * mm});
            skLineSegment(sketch, "E683.12", {"start": v(-218.35, 201.59) * mm, "end": v(-218.35, 195.49) * mm});
            skLineSegment(sketch, "E684.0", {"start": v(-407.5, 58.23) * mm, "end": v(-390.5, 58.23) * mm});
            skLineSegment(sketch, "E684.2", {"start": v(-457.26, 156.54) * mm, "end": v(-467.76, 138.36) * mm});
            skLineSegment(sketch, "E684.3", {"start": v(-390.5, 63.73) * mm, "end": v(-426.26, 179.08) * mm});
            skLineSegment(sketch, "E684.4", {"start": v(-463, 135.6) * mm, "end": v(-497.5, 75.85) * mm});
            skLineSegment(sketch, "E684.8", {"start": v(-459.5, 58.23) * mm, "end": v(-442.5, 58.23) * mm});
            skLineSegment(sketch, "E684.12", {"start": v(-390.5, 58.23) * mm, "end": v(-390.5, 63.73) * mm});
            skLineSegment(sketch, "E684.14", {"start": v(-452.5, 153.8) * mm, "end": v(-457.26, 156.54) * mm});
            skLineSegment(sketch, "E684.16", {"start": v(-467.76, 138.36) * mm, "end": v(-463, 135.6) * mm});
            skLineSegment(sketch, "E684.20", {"start": v(-459.5, 63.73) * mm, "end": v(-459.5, 58.23) * mm});
            skLineSegment(sketch, "E684.22", {"start": v(-442.5, 58.23) * mm, "end": v(-442.5, 63.73) * mm});
            skLineSegment(sketch, "E684.25", {"start": v(-407.5, 63.73) * mm, "end": v(-407.5, 58.23) * mm});
            skArc(sketch, "E684.27", {"start": v(-426.26, 179.08) * mm, "mid": v(-431.32, 183.27) * mm, "end": v(-437.19, 180.3) * mm});
            skLineSegment(sketch, "E685", {"start": v(-288.83, 287.44) * mm, "end": v(-288.83, 38.29) * mm, "construction": true});
            skLineSegment(sketch, "E686", {"start": v(-288.83, 114.41) * mm, "end": v(-218.35, 114.41) * mm, "construction": true});
            skPoint(sketch, "E687", {"position": v(-141.74, 114.41) * mm});
            skPoint(sketch, "E687.positionSnap0", {"position": v(-207.7, 114.41) * mm});
            skPoint(sketch, "E688", {"position": v(-504.5, 63.73) * mm});
            skPoint(sketch, "E689", {"position": v(-430.32, 192.19) * mm});
            skLineSegment(sketch, "E690.0", {"start": v(-465.74, -205.84) * mm, "end": v(-465.74, -230.92) * mm});
            skLineSegment(sketch, "E690.1", {"start": v(-675.14, -230.92) * mm, "end": v(-465.74, -230.92) * mm});
            skLineSegment(sketch, "E690.2", {"start": v(-675.14, -230.92) * mm, "end": v(-675.14, -205.84) * mm});
            skLineSegment(sketch, "E690.3", {"start": v(-675.14, -205.84) * mm, "end": v(-705, -154.13) * mm});
            skCircle(sketch, "E690.4", {"center": v(-570.44, -110.92) * mm, "radius": 15 * mm});
            skLineSegment(sketch, "E690.5", {"start": v(-705, -154.13) * mm, "end": v(-726.71, -141.6) * mm});
            skLineSegment(sketch, "E690.6", {"start": v(-570.66, -26.75) * mm, "end": v(-546.66, -68.32) * mm});
            skLineSegment(sketch, "E690.7", {"start": v(-546.66, -68.32) * mm, "end": v(-496.34, -39.27) * mm});
            skArc(sketch, "E690.8", {"start": v(-642.13, -81.08) * mm, "mid": v(-639.56, -90.64) * mm, "end": v(-630, -88.08) * mm});
            skArc(sketch, "E690.9", {"start": v(-620, -70.76) * mm, "mid": v(-622.56, -61.2) * mm, "end": v(-632.13, -63.76) * mm});
            skLineSegment(sketch, "E690.10", {"start": v(-570.44, -105.92) * mm, "end": v(-570.44, -93.42) * mm});
            skLineSegment(sketch, "E690.11", {"start": v(-575.44, -110.92) * mm, "end": v(-587.94, -110.92) * mm});
            skLineSegment(sketch, "E690.12", {"start": v(-570.44, -115.92) * mm, "end": v(-570.44, -128.42) * mm});
            skLineSegment(sketch, "E690.13", {"start": v(-565.44, -110.92) * mm, "end": v(-552.94, -110.92) * mm});
            skCircle(sketch, "E690.14", {"center": v(-665.7, -165.92) * mm, "radius": 1.65 * mm});
            skCircle(sketch, "E690.15", {"center": v(-475.18, -165.92) * mm, "radius": 1.65 * mm});
            skLineSegment(sketch, "E690.16", {"start": v(-608.31, -198.23) * mm, "end": v(-608.31, -185.22) * mm});
            skArc(sketch, "E690.17", {"start": v(-608.31, -185.22) * mm, "mid": v(-615.31, -178.22) * mm, "end": v(-622.31, -185.22) * mm});
            skLineSegment(sketch, "E690.18", {"start": v(-632.13, -63.76) * mm, "end": v(-642.13, -81.08) * mm});
            skLineSegment(sketch, "E690.19", {"start": v(-630, -88.08) * mm, "end": v(-620, -70.76) * mm});
            skLineSegment(sketch, "E690.20", {"start": v(-488.4, -107.96) * mm, "end": v(-491.45, -113.24) * mm});
            skLineSegment(sketch, "E690.21", {"start": v(-503.38, -99.3) * mm, "end": v(-488.4, -107.96) * mm});
            skLineSegment(sketch, "E690.22", {"start": v(-506.43, -104.6) * mm, "end": v(-503.38, -99.3) * mm});
            skLineSegment(sketch, "E690.23", {"start": v(-491.45, -113.24) * mm, "end": v(-506.43, -104.6) * mm});
            skLineSegment(sketch, "E690.24", {"start": v(-483.9, -204.17) * mm, "end": v(-486.95, -209.45) * mm});
            skLineSegment(sketch, "E690.25", {"start": v(-498.89, -195.52) * mm, "end": v(-483.9, -204.17) * mm});
            skLineSegment(sketch, "E690.26", {"start": v(-501.94, -200.8) * mm, "end": v(-498.89, -195.52) * mm});
            skLineSegment(sketch, "E690.27", {"start": v(-486.95, -209.45) * mm, "end": v(-501.94, -200.8) * mm});
            skLineSegment(sketch, "E690.28", {"start": v(-543.92, -169.52) * mm, "end": v(-528.94, -178.17) * mm});
            skLineSegment(sketch, "E690.29", {"start": v(-546.97, -174.8) * mm, "end": v(-543.92, -169.52) * mm});
            skLineSegment(sketch, "E690.30", {"start": v(-622.31, -185.22) * mm, "end": v(-622.31, -198.23) * mm});
            skLineSegment(sketch, "E690.31", {"start": v(-531.99, -183.45) * mm, "end": v(-546.97, -174.8) * mm});
            skArc(sketch, "E690.32", {"start": v(-622.31, -198.23) * mm, "mid": v(-615.31, -205.23) * mm, "end": v(-608.31, -198.23) * mm});
            skLineSegment(sketch, "E690.33", {"start": v(-528.94, -178.17) * mm, "end": v(-531.99, -183.45) * mm});
            skArc(sketch, "E690.34", {"start": v(-507.16, -143.01) * mm, "mid": v(-507.58, -140.93) * mm, "end": v(-509.66, -141.35) * mm});
            skLineSegment(sketch, "E690.35", {"start": v(-509.66, -141.35) * mm, "end": v(-512.43, -145.5) * mm});
            skArc(sketch, "E690.36", {"start": v(-512.43, -145.5) * mm, "mid": v(-512.01, -147.59) * mm, "end": v(-509.93, -147.17) * mm});
            skLineSegment(sketch, "E690.37", {"start": v(-503.7, -145.26) * mm, "end": v(-506.37, -149.48) * mm});
            skArc(sketch, "E690.38", {"start": v(-506.37, -149.48) * mm, "mid": v(-505.9, -151.55) * mm, "end": v(-503.83, -151.09) * mm});
            skArc(sketch, "E690.39", {"start": v(-637.1, -142.8) * mm, "mid": v(-635, -142.5) * mm, "end": v(-635.3, -140.4) * mm});
            skLineSegment(sketch, "E690.40", {"start": v(-635.3, -140.4) * mm, "end": v(-639.31, -137.4) * mm});
            skArc(sketch, "E690.41", {"start": v(-639.31, -137.4) * mm, "mid": v(-641.41, -137.7) * mm, "end": v(-641.1, -139.8) * mm});
            skArc(sketch, "E690.42", {"start": v(-640.7, -147.85) * mm, "mid": v(-638.61, -147.48) * mm, "end": v(-638.98, -145.4) * mm});
            skLineSegment(sketch, "E690.43", {"start": v(-638.98, -145.4) * mm, "end": v(-643.07, -142.52) * mm});
            skArc(sketch, "E690.44", {"start": v(-643.07, -142.52) * mm, "mid": v(-645.16, -142.89) * mm, "end": v(-644.8, -144.98) * mm});
            skLineSegment(sketch, "E690.45", {"start": v(-509.93, -147.17) * mm, "end": v(-507.16, -143.01) * mm});
            skArc(sketch, "E690.46", {"start": v(-577.35, -40.01) * mm, "mid": v(-575.38, -39.23) * mm, "end": v(-576.16, -37.25) * mm});
            skLineSegment(sketch, "E690.47", {"start": v(-576.16, -37.25) * mm, "end": v(-580.76, -35.28) * mm});
            skArc(sketch, "E690.48", {"start": v(-580.76, -35.28) * mm, "mid": v(-582.73, -36.06) * mm, "end": v(-581.94, -38.04) * mm});
            skLineSegment(sketch, "E690.49", {"start": v(-579.39, -32.22) * mm, "end": v(-574.85, -34.33) * mm});
            skLineSegment(sketch, "E690.50", {"start": v(-503.83, -151.09) * mm, "end": v(-501.16, -146.86) * mm});
            skArc(sketch, "E690.51", {"start": v(-574.85, -34.33) * mm, "mid": v(-572.86, -33.6) * mm, "end": v(-573.6, -31.6) * mm});
            skArc(sketch, "E690.52", {"start": v(-501.16, -146.86) * mm, "mid": v(-501.63, -144.79) * mm, "end": v(-503.7, -145.26) * mm});
            skLineSegment(sketch, "E690.53", {"start": v(-573.6, -31.6) * mm, "end": v(-578.12, -29.5) * mm});
            skArc(sketch, "E690.54", {"start": v(-578.12, -29.5) * mm, "mid": v(-580.12, -30.23) * mm, "end": v(-579.39, -32.22) * mm});
            skLineSegment(sketch, "E690.55", {"start": v(-641.1, -139.8) * mm, "end": v(-637.1, -142.8) * mm});
            skLineSegment(sketch, "E690.56", {"start": v(-644.8, -144.98) * mm, "end": v(-640.7, -147.85) * mm});
            skLineSegment(sketch, "E690.57", {"start": v(-581.94, -38.04) * mm, "end": v(-577.35, -40.01) * mm});
            skLineSegment(sketch, "E690.58", {"start": v(-664.07, -100.55) * mm, "end": v(-664.07, -99.05) * mm});
            skLineSegment(sketch, "E690.59", {"start": v(-661.57, -103.05) * mm, "end": v(-660.07, -103.05) * mm});
            skCircle(sketch, "E690.60", {"center": v(-698.2, -112.21) * mm, "radius": 2.5 * mm});
            skLineSegment(sketch, "E690.61", {"start": v(-698.2, -112.21) * mm, "end": v(-695.7, -112.21) * mm});
            skCircle(sketch, "E690.62", {"center": v(-664.07, -103.05) * mm, "radius": 1.5 * mm});
            skLineSegment(sketch, "E690.63", {"start": v(-698.2, -109.71) * mm, "end": v(-698.2, -107.21) * mm});
            skLineSegment(sketch, "E690.64", {"start": v(-700.7, -112.21) * mm, "end": v(-703.2, -112.21) * mm});
            skLineSegment(sketch, "E690.65", {"start": v(-698.2, -114.71) * mm, "end": v(-698.2, -117.21) * mm});
            skLineSegment(sketch, "E690.66", {"start": v(-695.7, -112.21) * mm, "end": v(-693.2, -112.21) * mm});
            skLineSegment(sketch, "E690.67", {"start": v(-621.57, -33.77) * mm, "end": v(-620.07, -33.77) * mm});
            skLineSegment(sketch, "E690.68", {"start": v(-570.44, -110.92) * mm, "end": v(-572.94, -110.92) * mm});
            skLineSegment(sketch, "E690.69", {"start": v(-570.44, -110.92) * mm, "end": v(-570.44, -113.42) * mm});
            skLineSegment(sketch, "E690.70", {"start": v(-570.44, -110.92) * mm, "end": v(-567.94, -110.92) * mm});
            skLineSegment(sketch, "E690.71", {"start": v(-664.07, -103.05) * mm, "end": v(-661.57, -103.05) * mm});
            skLineSegment(sketch, "E690.72", {"start": v(-666.57, -103.05) * mm, "end": v(-668.07, -103.05) * mm});
            skLineSegment(sketch, "E690.73", {"start": v(-664.07, -105.55) * mm, "end": v(-664.07, -107.05) * mm});
            skLineSegment(sketch, "E690.74", {"start": v(-698.2, -112.21) * mm, "end": v(-698.2, -109.71) * mm});
            skLineSegment(sketch, "E690.75", {"start": v(-698.2, -112.21) * mm, "end": v(-700.7, -112.21) * mm});
            skLineSegment(sketch, "E690.76", {"start": v(-698.2, -112.21) * mm, "end": v(-698.2, -114.71) * mm});
            skCircle(sketch, "E690.77", {"center": v(-624.07, -33.77) * mm, "radius": 1.5 * mm});
            skLineSegment(sketch, "E690.78", {"start": v(-624.07, -31.27) * mm, "end": v(-624.07, -29.77) * mm});
            skLineSegment(sketch, "E690.79", {"start": v(-626.57, -33.77) * mm, "end": v(-628.07, -33.77) * mm});
            skLineSegment(sketch, "E690.80", {"start": v(-624.07, -36.27) * mm, "end": v(-624.07, -37.77) * mm});
            skLineSegment(sketch, "E690.81", {"start": v(-512.5, -189.74) * mm, "end": v(-510.85, -189.74) * mm});
            skLineSegment(sketch, "E690.82", {"start": v(-570.44, -110.92) * mm, "end": v(-570.44, -108.42) * mm});
            skLineSegment(sketch, "E690.83", {"start": v(-664.07, -103.05) * mm, "end": v(-666.57, -103.05) * mm});
            skLineSegment(sketch, "E690.84", {"start": v(-664.07, -103.05) * mm, "end": v(-664.07, -105.55) * mm});
            skLineSegment(sketch, "E690.85", {"start": v(-474.47, -117.02) * mm, "end": v(-474.47, -115.37) * mm});
            skLineSegment(sketch, "E690.86", {"start": v(-637.94, -220.92) * mm, "end": v(-640.44, -220.92) * mm});
            skLineSegment(sketch, "E690.87", {"start": v(-579.96, -153.05) * mm, "end": v(-581.46, -153.05) * mm});
            skLineSegment(sketch, "E690.88", {"start": v(-476.97, -119.52) * mm, "end": v(-478.62, -119.52) * mm});
            skLineSegment(sketch, "E690.89", {"start": v(-577.46, -155.55) * mm, "end": v(-577.46, -157.05) * mm});
            skLineSegment(sketch, "E690.90", {"start": v(-632.94, -220.92) * mm, "end": v(-630.44, -220.92) * mm});
            skLineSegment(sketch, "E690.91", {"start": v(-471.97, -119.52) * mm, "end": v(-470.32, -119.52) * mm});
            skCircle(sketch, "E690.92", {"center": v(-474.47, -119.52) * mm, "radius": 1.65 * mm});
            skLineSegment(sketch, "E690.93", {"start": v(-624.07, -33.77) * mm, "end": v(-624.07, -31.27) * mm});
            skCircle(sketch, "E690.94", {"center": v(-537.46, -83.77) * mm, "radius": 1.5 * mm});
            skCircle(sketch, "E690.95", {"center": v(-635.44, -220.92) * mm, "radius": 2.5 * mm});
            skLineSegment(sketch, "E690.96", {"start": v(-624.07, -33.77) * mm, "end": v(-626.57, -33.77) * mm});
            skCircle(sketch, "E690.97", {"center": v(-577.46, -153.05) * mm, "radius": 1.5 * mm});
            skLineSegment(sketch, "E690.98", {"start": v(-624.07, -33.77) * mm, "end": v(-621.57, -33.77) * mm});
            skLineSegment(sketch, "E690.99", {"start": v(-537.46, -83.77) * mm, "end": v(-534.96, -83.77) * mm});
            skLineSegment(sketch, "E690.100", {"start": v(-515, -189.74) * mm, "end": v(-512.5, -189.74) * mm});
            skLineSegment(sketch, "E690.101", {"start": v(-537.46, -81.27) * mm, "end": v(-537.46, -79.77) * mm});
            skLineSegment(sketch, "E690.102", {"start": v(-515, -187.24) * mm, "end": v(-515, -185.59) * mm});
            skLineSegment(sketch, "E690.103", {"start": v(-539.96, -83.77) * mm, "end": v(-541.46, -83.77) * mm});
            skLineSegment(sketch, "E690.104", {"start": v(-517.5, -189.74) * mm, "end": v(-519.15, -189.74) * mm});
            skLineSegment(sketch, "E690.105", {"start": v(-537.46, -86.27) * mm, "end": v(-537.46, -87.77) * mm});
            skLineSegment(sketch, "E690.106", {"start": v(-515, -192.24) * mm, "end": v(-515, -193.89) * mm});
            skLineSegment(sketch, "E690.107", {"start": v(-534.96, -83.77) * mm, "end": v(-533.46, -83.77) * mm});
            skLineSegment(sketch, "E690.108", {"start": v(-664.07, -103.05) * mm, "end": v(-664.07, -100.55) * mm});
            skLineSegment(sketch, "E690.109", {"start": v(-635.44, -220.92) * mm, "end": v(-637.94, -220.92) * mm});
            skLineSegment(sketch, "E690.110", {"start": v(-474.47, -119.52) * mm, "end": v(-476.97, -119.52) * mm});
            skLineSegment(sketch, "E690.111", {"start": v(-635.44, -220.92) * mm, "end": v(-632.94, -220.92) * mm});
            skLineSegment(sketch, "E690.112", {"start": v(-577.46, -153.05) * mm, "end": v(-574.96, -153.05) * mm});
            skLineSegment(sketch, "E690.113", {"start": v(-474.47, -119.52) * mm, "end": v(-471.97, -119.52) * mm});
            skLineSegment(sketch, "E690.114", {"start": v(-577.46, -150.55) * mm, "end": v(-577.46, -149.05) * mm});
            skLineSegment(sketch, "E690.115", {"start": v(-635.44, -218.42) * mm, "end": v(-635.44, -215.92) * mm});
            skLineSegment(sketch, "E690.116", {"start": v(-635.44, -223.42) * mm, "end": v(-635.44, -225.92) * mm});
            skLineSegment(sketch, "E690.117", {"start": v(-474.47, -122.02) * mm, "end": v(-474.47, -123.67) * mm});
            skLineSegment(sketch, "E690.118", {"start": v(-574.96, -153.05) * mm, "end": v(-573.46, -153.05) * mm});
            skLineSegment(sketch, "E690.119", {"start": v(-515, -189.74) * mm, "end": v(-515, -187.24) * mm});
            skLineSegment(sketch, "E690.120", {"start": v(-515, -189.74) * mm, "end": v(-517.5, -189.74) * mm});
            skCircle(sketch, "E690.121", {"center": v(-505.44, -220.92) * mm, "radius": 2.5 * mm});
            skLineSegment(sketch, "E690.122", {"start": v(-624.07, -33.77) * mm, "end": v(-624.07, -36.27) * mm});
            skLineSegment(sketch, "E690.123", {"start": v(-537.46, -83.77) * mm, "end": v(-537.46, -86.27) * mm});
            skLineSegment(sketch, "E690.124", {"start": v(-515, -189.74) * mm, "end": v(-515, -192.24) * mm});
            skLineSegment(sketch, "E690.125", {"start": v(-505.44, -220.92) * mm, "end": v(-502.94, -220.92) * mm});
            skLineSegment(sketch, "E690.126", {"start": v(-505.44, -218.42) * mm, "end": v(-505.44, -215.92) * mm});
            skLineSegment(sketch, "E690.127", {"start": v(-507.94, -220.92) * mm, "end": v(-510.44, -220.92) * mm});
            skLineSegment(sketch, "E690.128", {"start": v(-505.44, -223.42) * mm, "end": v(-505.44, -225.92) * mm});
            skLineSegment(sketch, "E690.129", {"start": v(-502.94, -220.92) * mm, "end": v(-500.44, -220.92) * mm});
            skLineSegment(sketch, "E690.130", {"start": v(-635.44, -220.92) * mm, "end": v(-635.44, -218.42) * mm});
            skLineSegment(sketch, "E690.131", {"start": v(-577.46, -153.05) * mm, "end": v(-577.46, -150.55) * mm});
            skLineSegment(sketch, "E690.132", {"start": v(-635.44, -220.92) * mm, "end": v(-635.44, -223.42) * mm});
            skLineSegment(sketch, "E690.133", {"start": v(-577.46, -153.05) * mm, "end": v(-577.46, -155.55) * mm});
            skLineSegment(sketch, "E690.134", {"start": v(-474.47, -119.52) * mm, "end": v(-474.47, -122.02) * mm});
            skCircle(sketch, "E690.135", {"center": v(-515, -189.74) * mm, "radius": 1.65 * mm});
            skLineSegment(sketch, "E690.136", {"start": v(-505.44, -220.92) * mm, "end": v(-505.44, -218.42) * mm});
            skLineSegment(sketch, "E690.137", {"start": v(-537.46, -83.77) * mm, "end": v(-539.96, -83.77) * mm});
            skLineSegment(sketch, "E690.138", {"start": v(-505.44, -220.92) * mm, "end": v(-505.44, -223.42) * mm});
            skLineSegment(sketch, "E690.139", {"start": v(-474.47, -119.52) * mm, "end": v(-474.47, -117.02) * mm});
            skLineSegment(sketch, "E690.140", {"start": v(-577.46, -153.05) * mm, "end": v(-579.96, -153.05) * mm});
            skLineSegment(sketch, "E690.141", {"start": v(-537.46, -83.77) * mm, "end": v(-537.46, -81.27) * mm});
            skLineSegment(sketch, "E690.142", {"start": v(-505.44, -220.92) * mm, "end": v(-507.94, -220.92) * mm});
            skLineSegment(sketch, "E691.0", {"start": v(-435.89, -154.13) * mm, "end": v(-465.74, -205.84) * mm});
            skLineSegment(sketch, "E691.3", {"start": v(-414.17, -141.6) * mm, "end": v(-435.89, -154.13) * mm});
            skLineSegment(sketch, "E691.4", {"start": v(-414.17, -141.6) * mm, "end": v(-518.87, 39.75) * mm});
            skLineSegment(sketch, "E691.6", {"start": v(-443.37, -133.96) * mm, "end": v(-446.42, -139.24) * mm});
            skLineSegment(sketch, "E691.7", {"start": v(-458.35, -125.3) * mm, "end": v(-443.37, -133.96) * mm});
            skLineSegment(sketch, "E691.8", {"start": v(-461.4, -130.6) * mm, "end": v(-458.35, -125.3) * mm});
            skLineSegment(sketch, "E691.9", {"start": v(-446.42, -139.24) * mm, "end": v(-461.4, -130.6) * mm});
            skLineSegment(sketch, "E691.33", {"start": v(-442.68, -109.71) * mm, "end": v(-442.68, -107.21) * mm});
            skCircle(sketch, "E691.34", {"center": v(-442.68, -112.21) * mm, "radius": 2.5 * mm});
            skLineSegment(sketch, "E691.35", {"start": v(-445.18, -112.21) * mm, "end": v(-447.68, -112.21) * mm});
            skLineSegment(sketch, "E691.37", {"start": v(-442.68, -114.71) * mm, "end": v(-442.68, -117.21) * mm});
            skLineSegment(sketch, "E691.38", {"start": v(-440.18, -112.21) * mm, "end": v(-437.68, -112.21) * mm});
            skLineSegment(sketch, "E691.45", {"start": v(-442.68, -112.21) * mm, "end": v(-442.68, -114.71) * mm});
            skLineSegment(sketch, "E691.46", {"start": v(-442.68, -112.21) * mm, "end": v(-440.18, -112.21) * mm});
            skLineSegment(sketch, "E691.51", {"start": v(-442.68, -112.21) * mm, "end": v(-445.18, -112.21) * mm});
            skLineSegment(sketch, "E691.53", {"start": v(-442.68, -112.21) * mm, "end": v(-442.68, -109.71) * mm});
            skLineSegment(sketch, "E692.0", {"start": v(-496.34, -39.27) * mm, "end": v(-520.34, 2.3) * mm});
            skLineSegment(sketch, "E692.1", {"start": v(-540.59, 27.21) * mm, "end": v(-518.87, 39.75) * mm});
            skLineSegment(sketch, "E692.2", {"start": v(-520.34, 2.3) * mm, "end": v(-570.66, -26.75) * mm});
            skLineSegment(sketch, "E692.3", {"start": v(-622.01, 39.75) * mm, "end": v(-600.3, 27.21) * mm});
            skLineSegment(sketch, "E692.4", {"start": v(-600.3, 27.21) * mm, "end": v(-540.59, 27.21) * mm});
            skLineSegment(sketch, "E692.5", {"start": v(-622.01, 39.75) * mm, "end": v(-726.71, -141.6) * mm});
            skCircle(sketch, "E692.7", {"center": v(-570.44, -0.92) * mm, "radius": 1.65 * mm});
            skLineSegment(sketch, "E692.11", {"start": v(-630.7, 0.37) * mm, "end": v(-628.2, 0.37) * mm});
            skLineSegment(sketch, "E692.12", {"start": v(-633.2, 2.87) * mm, "end": v(-633.2, 5.37) * mm});
            skLineSegment(sketch, "E692.13", {"start": v(-507.68, 2.87) * mm, "end": v(-507.68, 5.37) * mm});
            skLineSegment(sketch, "E692.14", {"start": v(-510.18, 0.37) * mm, "end": v(-512.68, 0.37) * mm});
            skLineSegment(sketch, "E692.15", {"start": v(-505.18, 0.37) * mm, "end": v(-502.68, 0.37) * mm});
            skLineSegment(sketch, "E692.16", {"start": v(-633.2, 0.37) * mm, "end": v(-630.7, 0.37) * mm});
            skLineSegment(sketch, "E692.17", {"start": v(-635.7, 0.37) * mm, "end": v(-638.2, 0.37) * mm});
            skCircle(sketch, "E692.18", {"center": v(-507.68, 0.37) * mm, "radius": 2.5 * mm});
            skLineSegment(sketch, "E692.19", {"start": v(-633.2, -2.13) * mm, "end": v(-633.2, -4.63) * mm});
            skCircle(sketch, "E692.20", {"center": v(-633.2, 0.37) * mm, "radius": 2.5 * mm});
            skLineSegment(sketch, "E692.21", {"start": v(-507.68, 0.37) * mm, "end": v(-507.68, 2.87) * mm});
            skLineSegment(sketch, "E692.22", {"start": v(-507.68, 0.37) * mm, "end": v(-510.18, 0.37) * mm});
            skLineSegment(sketch, "E692.23", {"start": v(-507.68, 0.37) * mm, "end": v(-505.18, 0.37) * mm});
            skLineSegment(sketch, "E692.25", {"start": v(-507.68, -2.13) * mm, "end": v(-507.68, -4.63) * mm});
            skLineSegment(sketch, "E692.27", {"start": v(-633.2, 0.37) * mm, "end": v(-633.2, 2.87) * mm});
            skLineSegment(sketch, "E692.28", {"start": v(-633.2, 0.37) * mm, "end": v(-635.7, 0.37) * mm});
            skLineSegment(sketch, "E692.29", {"start": v(-633.2, 0.37) * mm, "end": v(-633.2, -2.13) * mm});
            skLineSegment(sketch, "E692.31", {"start": v(-507.68, 0.37) * mm, "end": v(-507.68, -2.13) * mm});
            skPoint(sketch, "E693", {"position": v(-444.5, 167.65) * mm});
            skPoint(sketch, "E694", {"position": v(-497.5, 75.85) * mm});
            skPoint(sketch, "E695", {"position": v(-404.5, 236.93) * mm});
            skPoint(sketch, "E696", {"position": v(-494.5, 63.73) * mm});
            skLineSegment(sketch, "E697", {"start": v(-490.5, 63.73) * mm, "end": v(-490.5, 67.23) * mm});
            skLineSegment(sketch, "E698", {"start": v(-490.5, 67.23) * mm, "end": v(-497.5, 67.23) * mm});
            skLineSegment(sketch, "E699", {"start": v(-497.5, 67.23) * mm, "end": v(-497.5, 63.73) * mm, "construction": true});
            skLineSegment(sketch, "E700", {"start": v(-490.5, 63.73) * mm, "end": v(-459.5, 63.73) * mm});
            skLineSegment(sketch, "E701", {"start": v(-504.5, 63.73) * mm, "end": v(-497.5, 63.73) * mm, "construction": true});
            skLineSegment(sketch, "E702", {"start": v(-497.5, 75.85) * mm, "end": v(-497.5, 67.23) * mm});
            skLineSegment(sketch, "E703", {"start": v(-488.4, -107.96) * mm, "end": v(-581.37, -54.28) * mm, "construction": true});
            skLineSegment(sketch, "E704", {"start": v(-496.34, -39.27) * mm, "end": v(-602.85, -100.77) * mm, "construction": true});
            skPoint(sketch, "E705", {"position": v(-547.52, -73.82) * mm});
            skPoint(sketch, "E706", {"position": v(-551.85, -71.32) * mm});
            skLineSegment(sketch, "E707", {"start": v(-442.5, 63.73) * mm, "end": v(-407.5, 63.73) * mm});
            skPoint(sketch, "E708", {"position": v(-424.5, 63.73) * mm});
            skPoint(sketch, "E709", {"position": v(-450.2, 157.75) * mm});
            skLineSegment(sketch, "E710", {"start": v(-452.5, 153.8) * mm, "end": v(-437.19, 180.3) * mm});
            skCircle(sketch, "E711", {"center": v(-439.9, 111.28) * mm, "radius": 72.5 * mm, "construction": true});
            skPoint(sketch, "E712", {"position": v(-431.28, 183.26) * mm});
            skLineSegment(sketch, "E713.0", {"start": v(-452.6, 73.73) * mm, "end": v(-410.85, 73.73) * mm});
            skLineSegment(sketch, "E713.1", {"start": v(-478.51, 73.73) * mm, "end": v(-452.6, 73.73) * mm});
            skLineSegment(sketch, "E713.2", {"start": v(-465.12, 111.92) * mm, "end": v(-438.82, 157.47) * mm});
            skLineSegment(sketch, "E713.3", {"start": v(-465.12, 111.92) * mm, "end": v(-482.84, 81.23) * mm});
            skLineSegment(sketch, "E713.5", {"start": v(-406.07, 80.2) * mm, "end": v(-429.71, 156.45) * mm});
            skPoint(sketch, "E714.visualSharp", {"position": v(-404.06, 73.73) * mm});
            skArc(sketch, "E714.filletArc", {"start": v(-410.85, 73.73) * mm, "mid": v(-406.82, 75.76) * mm, "end": v(-406.07, 80.2) * mm});
            skPoint(sketch, "E715.visualSharp", {"position": v(-433.1, 167.38) * mm});
            skArc(sketch, "E715.filletArc", {"start": v(-429.71, 156.45) * mm, "mid": v(-433.93, 159.94) * mm, "end": v(-438.82, 157.47) * mm});
            skArc(sketch, "E716", {"start": v(-482.84, 81.23) * mm, "mid": v(-482.84, 76.23) * mm, "end": v(-478.51, 73.73) * mm});
            skPoint(sketch, "E717", {"position": v(-484.5, 98.37) * mm});
            skSolve(sketch);
        }
        {
            var Q0;
            Q0=qSketchRegion(id+"F1",true);
            extrude(context, id + "F2", {"entities" : qUnion([Q0]), "depth" : 6 * mm});
        }
        {
            var Q0;
            Q0=makeQuery(id+"F2.opExtrude","CAP_FACE",FACE,{"disambiguationData":[OSD([sQuery(id+"F1.wireOp",EDGE,"E684.0"),sQuery(id+"F1.wireOp",EDGE,"E684.2"),sQuery(id+"F1.wireOp",EDGE,"E684.3"),sQuery(id+"F1.wireOp",EDGE,"E684.4"),sQuery(id+"F1.wireOp",EDGE,"E684.8"),sQuery(id+"F1.wireOp",EDGE,"E684.12"),sQuery(id+"F1.wireOp",EDGE,"E684.14"),sQuery(id+"F1.wireOp",EDGE,"E684.16"),sQuery(id+"F1.wireOp",EDGE,"E684.20"),sQuery(id+"F1.wireOp",EDGE,"E684.22"),sQuery(id+"F1.wireOp",EDGE,"E684.25"),sQuery(id+"F1.wireOp",EDGE,"E684.27"),sQuery(id+"F1.wireOp",EDGE,"E697"),sQuery(id+"F1.wireOp",EDGE,"E698"),sQuery(id+"F1.wireOp",EDGE,"E700"),sQuery(id+"F1.wireOp",EDGE,"E702"),sQuery(id+"F1.wireOp",EDGE,"E707"),sQuery(id+"F1.wireOp",EDGE,"E710"),sQuery(id+"F1.wireOp",EDGE,"E713.0"),sQuery(id+"F1.wireOp",EDGE,"E713.1"),sQuery(id+"F1.wireOp",EDGE,"E713.2"),sQuery(id+"F1.wireOp",EDGE,"E713.3"),sQuery(id+"F1.wireOp",EDGE,"E713.5"),sQuery(id+"F1.wireOp",EDGE,"E714.filletArc"),sQuery(id+"F1.wireOp",EDGE,"E715.filletArc"),sQuery(id+"F1.wireOp",EDGE,"E716")])],"isStart":false});
            var sketch = newSketch(context, id + "F3", { "sketchPlane" : qUnion([Q0])});
            skLineSegment(sketch, "E718.0.4", {"start": v(-490.5, 67.23) * mm, "end": v(-490.5, 63.73) * mm});
            skLineSegment(sketch, "E718.0.13", {"start": v(-396.52, 83.17) * mm, "end": v(-426.26, 179.08) * mm});
            skArc(sketch, "E718.0.14", {"start": v(-426.26, 179.08) * mm, "mid": v(-431.32, 183.27) * mm, "end": v(-437.19, 180.3) * mm});
            skLineSegment(sketch, "E719", {"start": v(-478.51, 63.73) * mm, "end": v(-410.85, 63.73) * mm});
            skArc(sketch, "E720.2", {"start": v(-428.65, 178.34) * mm, "mid": v(-431.6, 180.78) * mm, "end": v(-435.02, 179.05) * mm});
            skLineSegment(sketch, "E720.3", {"start": v(-398.9, 82.43) * mm, "end": v(-428.65, 178.34) * mm});
            skLineSegment(sketch, "E720.4", {"start": v(-478.51, 66.23) * mm, "end": v(-410.85, 66.23) * mm});
            skLineSegment(sketch, "E720.5", {"start": v(-489.34, 84.98) * mm, "end": v(-435.02, 179.05) * mm});
            skArc(sketch, "E721", {"start": v(-489.34, 84.98) * mm, "mid": v(-489.34, 72.48) * mm, "end": v(-478.51, 66.23) * mm});
            skArc(sketch, "E722", {"start": v(-491.5, 86.23) * mm, "mid": v(-491.5, 71.23) * mm, "end": v(-478.51, 63.73) * mm});
            skLineSegment(sketch, "E723", {"start": v(-491.5, 86.23) * mm, "end": v(-437.19, 180.3) * mm});
            skPoint(sketch, "E724.visualSharp", {"position": v(-393.89, 66.23) * mm});
            skArc(sketch, "E724.filletArc", {"start": v(-410.85, 66.23) * mm, "mid": v(-400.79, 71.31) * mm, "end": v(-398.9, 82.43) * mm});
            skPoint(sketch, "E725.visualSharp", {"position": v(-390.5, 63.73) * mm});
            skArc(sketch, "E725.filletArc", {"start": v(-410.85, 63.73) * mm, "mid": v(-398.77, 69.83) * mm, "end": v(-396.52, 83.17) * mm});
            skSolve(sketch);
        }
        {
            var Q0;
            Q0=makeQuery(id+"F3.imprint","IMPRINT",FACE,{"disambiguationData":[TD([[makeQuery(id+"F3.imprint","IMPRINT",EDGE,{"derivedFrom":sQuery(id+"F3.wireOp",EDGE,"E718.0.13")}),1.0]])]});
            extrude(context, id + "F4", {"entities" : qUnion([Q0]), "operationType" : NewBodyOperationType.ADD, "depth" : 4 * mm});
        }
        {
            var Q0;
            Q0=makeQuery(id+"F4.boolean.opBoolean","MERGE",FACE,{"derivedFrom":[makeQuery(id+"F2.opExtrude","SWEPT_FACE",FACE,{"disambiguationData":[OSD([sQuery(id+"F1.wireOp",EDGE,"E700")])]}),makeQuery(id+"F2.opExtrude","SWEPT_FACE",FACE,{"disambiguationData":[OSD([sQuery(id+"F1.wireOp",EDGE,"E707")])]}),makeQuery(id+"F4.opExtrude","SWEPT_FACE",FACE,{"disambiguationData":[OSD([sQuery(id+"F3.wireOp",EDGE,"E719")])]})]});
            var sketch = newSketch(context, id + "F5", { "sketchPlane" : qUnion([Q0])});
            skPoint(sketch, "E726.0", {"position": v(-424.5, 0) * mm});
            skLineSegment(sketch, "E727.0.0", {"start": v(-442.5, 0) * mm, "end": v(-407.5, 0) * mm});
            skPoint(sketch, "E728", {"position": v(-442.5, 86.45) * mm});
            skLineSegment(sketch, "E729", {"start": v(-424.5, 0) * mm, "end": v(-424.5, 6) * mm, "construction": true});
            skCircle(sketch, "E730", {"center": v(-424.5, 3) * mm, "radius": 1.57 * mm});
            skSolve(sketch);
        }
        {
            var Q0;
            Q0=makeQuery(id+"F2.opExtrude","SWEPT_FACE",FACE,{"disambiguationData":[OSD([sQuery(id+"F1.wireOp",EDGE,"E710")])]});
            var sketch = newSketch(context, id + "F6", { "sketchPlane" : qUnion([Q0])});
            skLineSegment(sketch, "E731", {"start": v(88.48, 0) * mm, "end": v(88.48, 6) * mm, "construction": true});
            skCircle(sketch, "E732", {"center": v(88.48, 3) * mm, "radius": 1.57 * mm});
            skSolve(sketch);
        }
        {
            var Q0;
            Q0=sQuery(id+"F6.wireOp",VERTEX,"E732.center");
            var Q1;
            Q1=sQuery(id+"F5.wireOp",VERTEX,"E730.center");
            var Q2;
            Q2=makeQuery(id+"F2.opExtrude","SWEPT_BODY",BODY,{"disambiguationData":[OSD([sQuery(id+"F1.wireOp",EDGE,"E684.0"),sQuery(id+"F1.wireOp",EDGE,"E684.2"),sQuery(id+"F1.wireOp",EDGE,"E684.3"),sQuery(id+"F1.wireOp",EDGE,"E684.4"),sQuery(id+"F1.wireOp",EDGE,"E684.8"),sQuery(id+"F1.wireOp",EDGE,"E684.12"),sQuery(id+"F1.wireOp",EDGE,"E684.14"),sQuery(id+"F1.wireOp",EDGE,"E684.16"),sQuery(id+"F1.wireOp",EDGE,"E684.20"),sQuery(id+"F1.wireOp",EDGE,"E684.22"),sQuery(id+"F1.wireOp",EDGE,"E684.25"),sQuery(id+"F1.wireOp",EDGE,"E684.27"),sQuery(id+"F1.wireOp",EDGE,"E697"),sQuery(id+"F1.wireOp",EDGE,"E698"),sQuery(id+"F1.wireOp",EDGE,"E700"),sQuery(id+"F1.wireOp",EDGE,"E702"),sQuery(id+"F1.wireOp",EDGE,"E707"),sQuery(id+"F1.wireOp",EDGE,"E710"),sQuery(id+"F1.wireOp",EDGE,"E713.0"),sQuery(id+"F1.wireOp",EDGE,"E713.1"),sQuery(id+"F1.wireOp",EDGE,"E713.2"),sQuery(id+"F1.wireOp",EDGE,"E713.3"),sQuery(id+"F1.wireOp",EDGE,"E713.5"),sQuery(id+"F1.wireOp",EDGE,"E714.filletArc"),sQuery(id+"F1.wireOp",EDGE,"E715.filletArc"),sQuery(id+"F1.wireOp",EDGE,"E716")])]});
            hole(context, id + "F7", {"style" : HoleStyle.SIMPLE, "endStyle" : HoleEndStyle.BLIND, "holeDiameter" : 3.15 * mm, "holeDepth" : 25 * mm, "locations" : qUnion([Q0, Q1]), "scope" : qUnion([Q2])});
        }
        {
            var Q0;
            Q0=makeQuery(id+"F7.hole-1.boolean.opBoolean","COPY",FACE,{"derivedFrom":makeQuery(id+"F7.hole-1.opRevolve","SWEPT_FACE",FACE,{"disambiguationData":[OSD([sQuery(id+"F7.hole-1.sketch.wireOp",EDGE,"core_line_2")])]})});
            var Q1;
            Q1=makeQuery(id+"F7.hole-0.boolean.opBoolean","COPY",FACE,{"derivedFrom":makeQuery(id+"F7.hole-0.opRevolve","SWEPT_FACE",FACE,{"disambiguationData":[OSD([sQuery(id+"F7.hole-0.sketch.wireOp",EDGE,"core_line_2")])]})});
            var Q2;
            Q2=makeQuery(id+"F4.opExtrude","CAP_FACE",FACE,{"disambiguationData":[OSD([sQuery(id+"F3.wireOp",EDGE,"E718.0.13"),sQuery(id+"F3.wireOp",EDGE,"E718.0.14"),sQuery(id+"F3.wireOp",EDGE,"E719"),sQuery(id+"F3.wireOp",EDGE,"E720.2"),sQuery(id+"F3.wireOp",EDGE,"E720.3"),sQuery(id+"F3.wireOp",EDGE,"E720.4"),sQuery(id+"F3.wireOp",EDGE,"E720.5"),sQuery(id+"F3.wireOp",EDGE,"E721"),sQuery(id+"F3.wireOp",EDGE,"E722"),sQuery(id+"F3.wireOp",EDGE,"E723"),sQuery(id+"F3.wireOp",EDGE,"E724.filletArc"),sQuery(id+"F3.wireOp",EDGE,"E725.filletArc")])],"isStart":false});
            var Q3;
            {var subQ0=sQuery(id+"F1.wireOp",EDGE,"E716");var subQ1=sQuery(id+"F1.wireOp",EDGE,"E715.filletArc");var subQ2=sQuery(id+"F1.wireOp",EDGE,"E713.1");var subQ3=sQuery(id+"F1.wireOp",EDGE,"E713.0");var subQ4=sQuery(id+"F1.wireOp",EDGE,"E713.3");var subQ5=sQuery(id+"F1.wireOp",EDGE,"E713.2");var subQ6=sQuery(id+"F1.wireOp",EDGE,"E713.5");var subQ7=sQuery(id+"F1.wireOp",EDGE,"E714.filletArc");Q3=makeQuery(id+"F4.boolean.opBoolean","SPLIT",FACE,{"disambiguationData":[TD([makeQuery(id+"F2.opExtrude","SWEPT_FACE",FACE,{"disambiguationData":[OSD([subQ6])]})])],"derivedFrom":makeQuery(id+"F2.opExtrude","CAP_FACE",FACE,{"disambiguationData":[OSD([sQuery(id+"F1.wireOp",EDGE,"E684.0"),sQuery(id+"F1.wireOp",EDGE,"E684.2"),sQuery(id+"F1.wireOp",EDGE,"E684.3"),sQuery(id+"F1.wireOp",EDGE,"E684.4"),sQuery(id+"F1.wireOp",EDGE,"E684.8"),sQuery(id+"F1.wireOp",EDGE,"E684.12"),sQuery(id+"F1.wireOp",EDGE,"E684.14"),sQuery(id+"F1.wireOp",EDGE,"E684.16"),sQuery(id+"F1.wireOp",EDGE,"E684.20"),sQuery(id+"F1.wireOp",EDGE,"E684.22"),sQuery(id+"F1.wireOp",EDGE,"E684.25"),sQuery(id+"F1.wireOp",EDGE,"E684.27"),sQuery(id+"F1.wireOp",EDGE,"E697"),sQuery(id+"F1.wireOp",EDGE,"E698"),sQuery(id+"F1.wireOp",EDGE,"E700"),sQuery(id+"F1.wireOp",EDGE,"E702"),sQuery(id+"F1.wireOp",EDGE,"E707"),sQuery(id+"F1.wireOp",EDGE,"E710"),subQ3,subQ2,subQ5,subQ4,subQ6,subQ7,subQ1,subQ0])],"isStart":false})});}
            var Q4;
            {var subQ0=sQuery(id+"F1.wireOp",EDGE,"E684.25");var subQ1=sQuery(id+"F1.wireOp",EDGE,"E707");var subQ2=sQuery(id+"F1.wireOp",EDGE,"E684.12");var subQ3=sQuery(id+"F1.wireOp",EDGE,"E684.3");var subQ4=sQuery(id+"F1.wireOp",EDGE,"E684.0");var subQ5=sQuery(id+"F1.wireOp",EDGE,"E700");Q4=makeQuery(id+"F4.boolean.opBoolean","SPLIT",FACE,{"disambiguationData":[TD([makeQuery(id+"F2.opExtrude","SWEPT_FACE",FACE,{"disambiguationData":[OSD([subQ4])]})])],"derivedFrom":makeQuery(id+"F2.opExtrude","CAP_FACE",FACE,{"disambiguationData":[OSD([subQ4,sQuery(id+"F1.wireOp",EDGE,"E684.2"),subQ3,sQuery(id+"F1.wireOp",EDGE,"E684.4"),sQuery(id+"F1.wireOp",EDGE,"E684.8"),subQ2,sQuery(id+"F1.wireOp",EDGE,"E684.14"),sQuery(id+"F1.wireOp",EDGE,"E684.16"),sQuery(id+"F1.wireOp",EDGE,"E684.20"),sQuery(id+"F1.wireOp",EDGE,"E684.22"),subQ0,sQuery(id+"F1.wireOp",EDGE,"E684.27"),sQuery(id+"F1.wireOp",EDGE,"E697"),sQuery(id+"F1.wireOp",EDGE,"E698"),subQ5,sQuery(id+"F1.wireOp",EDGE,"E702"),subQ1,sQuery(id+"F1.wireOp",EDGE,"E710"),sQuery(id+"F1.wireOp",EDGE,"E713.0"),sQuery(id+"F1.wireOp",EDGE,"E713.1"),sQuery(id+"F1.wireOp",EDGE,"E713.2"),sQuery(id+"F1.wireOp",EDGE,"E713.3"),sQuery(id+"F1.wireOp",EDGE,"E713.5"),sQuery(id+"F1.wireOp",EDGE,"E714.filletArc"),sQuery(id+"F1.wireOp",EDGE,"E715.filletArc"),sQuery(id+"F1.wireOp",EDGE,"E716")])],"isStart":false})});}
            var Q5;
            Q5=makeQuery(id+"F2.opExtrude","SWEPT_EDGE",EDGE,{"disambiguationData":[OSD([sQuery(id+"F1.wireOp",EDGE,"E684.0"),sQuery(id+"F1.wireOp",EDGE,"E684.25")])]});
            var Q6;
            Q6=makeQuery(id+"F2.opExtrude","SWEPT_EDGE",EDGE,{"disambiguationData":[OSD([sQuery(id+"F1.wireOp",EDGE,"E684.0"),sQuery(id+"F1.wireOp",EDGE,"E684.12")])]});
            var Q7;
            Q7=makeQuery(id+"F2.opExtrude","SWEPT_EDGE",EDGE,{"disambiguationData":[OSD([sQuery(id+"F1.wireOp",EDGE,"E684.8"),sQuery(id+"F1.wireOp",EDGE,"E684.22")])]});
            var Q8;
            Q8=makeQuery(id+"F2.opExtrude","SWEPT_EDGE",EDGE,{"disambiguationData":[OSD([sQuery(id+"F1.wireOp",EDGE,"E684.8"),sQuery(id+"F1.wireOp",EDGE,"E684.20")])]});
            var Q9;
            Q9=makeQuery(id+"F2.opExtrude","SWEPT_EDGE",EDGE,{"disambiguationData":[OSD([sQuery(id+"F1.wireOp",EDGE,"E697"),sQuery(id+"F1.wireOp",EDGE,"E700")])]});
            var Q10;
            Q10=makeQuery(id+"F2.opExtrude","CAP_EDGE",EDGE,{"disambiguationData":[OSD([sQuery(id+"F1.wireOp",EDGE,"E700")])],"isStart":false});
            var Q11;
            Q11=makeQuery(id+"F2.opExtrude","CAP_EDGE",EDGE,{"disambiguationData":[OSD([sQuery(id+"F1.wireOp",EDGE,"E697")])],"isStart":false});
            var Q12;
            Q12=makeQuery(id+"F2.opExtrude","SWEPT_EDGE",EDGE,{"disambiguationData":[OSD([sQuery(id+"F1.wireOp",EDGE,"E697"),sQuery(id+"F1.wireOp",EDGE,"E698")])]});
            var Q13;
            Q13=makeQuery(id+"F2.opExtrude","CAP_EDGE",EDGE,{"disambiguationData":[OSD([sQuery(id+"F1.wireOp",EDGE,"E698")])],"isStart":false});
            var Q14;
            Q14=makeQuery(id+"F2.opExtrude","SWEPT_EDGE",EDGE,{"disambiguationData":[OSD([sQuery(id+"F1.wireOp",EDGE,"E698"),sQuery(id+"F1.wireOp",EDGE,"E702")])]});
            var Q15;
            Q15=makeQuery(id+"F2.opExtrude","CAP_EDGE",EDGE,{"disambiguationData":[OSD([sQuery(id+"F1.wireOp",EDGE,"E702")])],"isStart":false});
            var Q16;
            Q16=makeQuery(id+"F2.opExtrude","CAP_EDGE",EDGE,{"disambiguationData":[OSD([sQuery(id+"F1.wireOp",EDGE,"E684.4")])],"isStart":false});
            var Q17;
            Q17=makeQuery(id+"F2.opExtrude","SWEPT_EDGE",EDGE,{"disambiguationData":[OSD([sQuery(id+"F1.wireOp",EDGE,"E684.4"),sQuery(id+"F1.wireOp",EDGE,"E702")])]});
            var Q18;
            Q18=makeQuery(id+"F2.opExtrude","CAP_EDGE",EDGE,{"disambiguationData":[OSD([sQuery(id+"F1.wireOp",EDGE,"E684.8")])],"isStart":false});
            var Q19;
            Q19=makeQuery(id+"F2.opExtrude","CAP_EDGE",EDGE,{"disambiguationData":[OSD([sQuery(id+"F1.wireOp",EDGE,"E684.16")])],"isStart":false});
            var Q20;
            Q20=makeQuery(id+"F2.opExtrude","CAP_EDGE",EDGE,{"disambiguationData":[OSD([sQuery(id+"F1.wireOp",EDGE,"E684.2")])],"isStart":false});
            var Q21;
            Q21=makeQuery(id+"F2.opExtrude","SWEPT_EDGE",EDGE,{"disambiguationData":[OSD([sQuery(id+"F1.wireOp",EDGE,"E684.2"),sQuery(id+"F1.wireOp",EDGE,"E684.16")])]});
            var Q22;
            Q22=makeQuery(id+"F2.opExtrude","SWEPT_EDGE",EDGE,{"disambiguationData":[OSD([sQuery(id+"F1.wireOp",EDGE,"E684.2"),sQuery(id+"F1.wireOp",EDGE,"E684.14")])]});
            var Q23;
            Q23=makeQuery(id+"F2.opExtrude","CAP_EDGE",EDGE,{"disambiguationData":[OSD([sQuery(id+"F1.wireOp",EDGE,"E684.14")])],"isStart":false});
            var Q24;
            Q24=makeQuery(id+"F4.opExtrude","CAP_EDGE",EDGE,{"disambiguationData":[OSD([sQuery(id+"F3.wireOp",EDGE,"E722")])],"isStart":true});
            fillet(context, id + "F8", {"entities" : qUnion([Q0, Q1, Q2, Q3, Q4, Q5, Q6, Q7, Q8, Q9, Q10, Q11, Q12, Q13, Q14, Q15, Q16, Q17, Q18, Q19, Q20, Q21, Q22, Q23, Q24]), "radius" : 1 * mm, "allowEdgeOverflow" : false});
        }
    });
